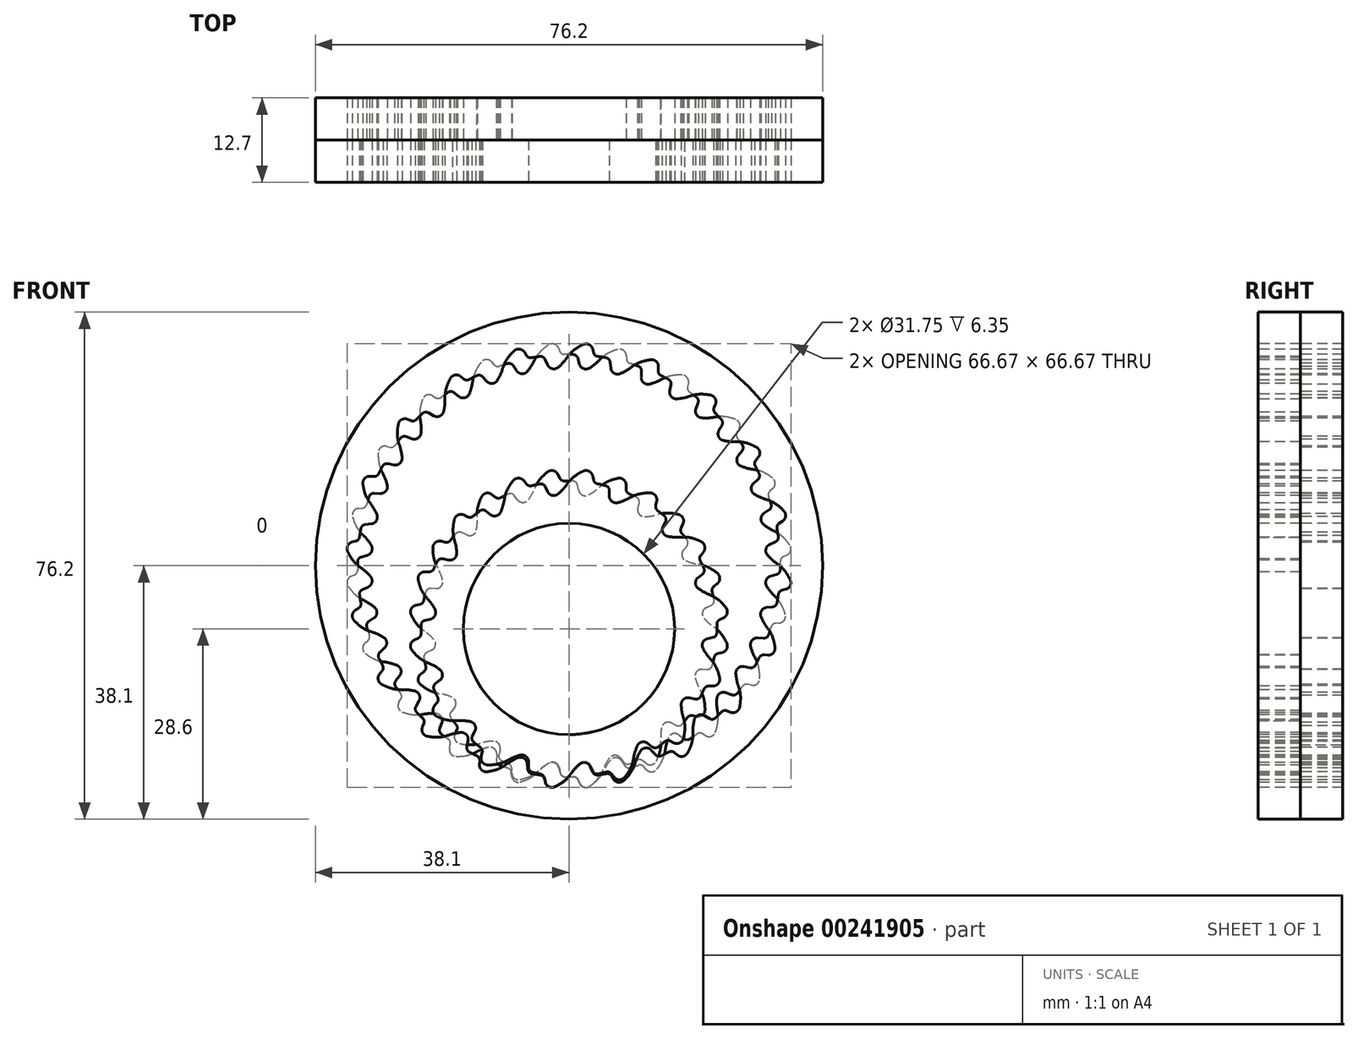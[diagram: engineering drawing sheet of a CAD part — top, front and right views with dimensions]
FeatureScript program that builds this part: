
annotation { "Feature Type Name" : "Feature", "Feature Type Description" : "" }
export const myFeature = defineFeature(function(context is Context, id is Id, definition is map)
    precondition{}
    {
        {
            var Q0;
            Q0=qCreatedBy(makeId("Front.planeOp"),FACE);
            var sketch = newSketch(context, id + "F0", { "sketchPlane" : qUnion([Q0])});
            skCircle(sketch, "E0", {"center": v(0, 0) * mm, "radius": 38.1 * mm});
            skCircle(sketch, "E1", {"center": v(0, 0) * mm, "radius": 31.75 * mm});
            skCircle(sketch, "E2", {"center": v(0, 0) * mm, "radius": 22.23 * mm});
            skCircle(sketch, "E3", {"center": v(0, 0) * mm, "radius": 15.88 * mm});
            skLineSegment(sketch, "E4", {"start": v(2.7, -19.53) * mm, "end": v(3.8, -21.9) * mm});
            skLineSegment(sketch, "E5", {"start": v(-3.3, -24.13) * mm, "end": v(-3.8, -21.9) * mm});
            skLineSegment(sketch, "E6", {"start": v(2.7, -29.06) * mm, "end": v(3.8, -31.52) * mm});
            skLineSegment(sketch, "E7", {"start": v(-3.3, -33.66) * mm, "end": v(-3.8, -31.52) * mm});
            skArc(sketch, "E8", {"start": v(2.7, -19.53) * mm, "mid": v(1.17, -20.7) * mm, "end": v(0, -22.23) * mm});
            skArc(sketch, "E9", {"start": v(-3.3, -24.13) * mm, "mid": v(-1.52, -23.4) * mm, "end": v(0, -22.23) * mm});
            skArc(sketch, "E10", {"start": v(-3.3, -33.66) * mm, "mid": v(-1.52, -32.92) * mm, "end": v(0, -31.75) * mm});
            skArc(sketch, "E11", {"start": v(2.7, -29.06) * mm, "mid": v(1.17, -30.22) * mm, "end": v(0, -31.75) * mm});
            skLineSegment(sketch, "E12.1.0", {"start": v(7.5, -23.17) * mm, "end": v(6.08, -21.38) * mm});
            skArc(sketch, "E12.1.1", {"start": v(7.5, -23.17) * mm, "mid": v(8.78, -21.74) * mm, "end": v(9.64, -20.02) * mm});
            skArc(sketch, "E12.1.2", {"start": v(10.9, -16.43) * mm, "mid": v(10.03, -18.14) * mm, "end": v(9.64, -20.02) * mm});
            skLineSegment(sketch, "E12.1.3", {"start": v(10.9, -16.43) * mm, "end": v(12.92, -18.08) * mm});
            skLineSegment(sketch, "E12.2.0", {"start": v(16.8, -17.62) * mm, "end": v(14.75, -16.62) * mm});
            skArc(sketch, "E12.2.1", {"start": v(16.8, -17.62) * mm, "mid": v(17.34, -15.78) * mm, "end": v(17.38, -13.86) * mm});
            skArc(sketch, "E12.2.2", {"start": v(16.95, -10.07) * mm, "mid": v(16.91, -12) * mm, "end": v(17.38, -13.86) * mm});
            skLineSegment(sketch, "E12.2.3", {"start": v(16.95, -10.07) * mm, "end": v(19.49, -10.69) * mm});
            skLineSegment(sketch, "E12.3.0", {"start": v(22.8, -8.59) * mm, "end": v(20.5, -8.57) * mm});
            skArc(sketch, "E12.3.1", {"start": v(22.8, -8.59) * mm, "mid": v(22.47, -6.7) * mm, "end": v(21.67, -4.95) * mm});
            skArc(sketch, "E12.3.2", {"start": v(19.64, -1.72) * mm, "mid": v(20.44, -3.47) * mm, "end": v(21.67, -4.95) * mm});
            skLineSegment(sketch, "E12.3.3", {"start": v(19.64, -1.72) * mm, "end": v(22.2, -1.17) * mm});
            skLineSegment(sketch, "E12.4.0", {"start": v(24.26, 2.15) * mm, "end": v(22.2, 1.17) * mm});
            skArc(sketch, "E12.4.1", {"start": v(24.26, 2.15) * mm, "mid": v(23.15, 3.72) * mm, "end": v(21.67, 4.95) * mm});
            skArc(sketch, "E12.4.2", {"start": v(18.44, 6.97) * mm, "mid": v(19.92, 5.74) * mm, "end": v(21.67, 4.95) * mm});
            skLineSegment(sketch, "E12.4.3", {"start": v(18.44, 6.97) * mm, "end": v(20.5, 8.57) * mm});
            skLineSegment(sketch, "E12.5.0", {"start": v(20.92, 12.47) * mm, "end": v(19.49, 10.69) * mm});
            skArc(sketch, "E12.5.1", {"start": v(20.92, 12.47) * mm, "mid": v(19.24, 13.4) * mm, "end": v(17.38, 13.86) * mm});
            skArc(sketch, "E12.5.2", {"start": v(13.6, 14.28) * mm, "mid": v(15.45, 13.82) * mm, "end": v(17.38, 13.86) * mm});
            skLineSegment(sketch, "E12.5.3", {"start": v(13.6, 14.28) * mm, "end": v(14.75, 16.62) * mm});
            skLineSegment(sketch, "E12.6.0", {"start": v(13.44, 20.3) * mm, "end": v(12.92, 18.08) * mm});
            skArc(sketch, "E12.6.1", {"start": v(13.44, 20.3) * mm, "mid": v(11.52, 20.42) * mm, "end": v(9.64, 20.02) * mm});
            skArc(sketch, "E12.6.2", {"start": v(6.05, 18.77) * mm, "mid": v(7.93, 19.16) * mm, "end": v(9.64, 20.02) * mm});
            skLineSegment(sketch, "E12.6.3", {"start": v(6.05, 18.77) * mm, "end": v(6.08, 21.38) * mm});
            skLineSegment(sketch, "E12.7.0", {"start": v(3.3, 24.13) * mm, "end": v(3.8, 21.9) * mm});
            skArc(sketch, "E12.7.1", {"start": v(3.3, 24.13) * mm, "mid": v(1.52, 23.4) * mm, "end": v(0, 22.23) * mm});
            skArc(sketch, "E12.7.2", {"start": v(-2.7, 19.53) * mm, "mid": v(-1.17, 20.7) * mm, "end": v(0, 22.22) * mm});
            skLineSegment(sketch, "E12.7.3", {"start": v(-2.7, 19.53) * mm, "end": v(-3.8, 21.9) * mm});
            skLineSegment(sketch, "E12.8.0", {"start": v(-7.5, 23.17) * mm, "end": v(-6.08, 21.38) * mm});
            skArc(sketch, "E12.8.1", {"start": v(-7.5, 23.17) * mm, "mid": v(-8.78, 21.74) * mm, "end": v(-9.64, 20.02) * mm});
            skArc(sketch, "E12.8.2", {"start": v(-10.9, 16.43) * mm, "mid": v(-10.03, 18.14) * mm, "end": v(-9.64, 20.02) * mm});
            skLineSegment(sketch, "E12.8.3", {"start": v(-10.9, 16.43) * mm, "end": v(-12.92, 18.08) * mm});
            skLineSegment(sketch, "E12.9.0", {"start": v(-16.8, 17.62) * mm, "end": v(-14.75, 16.62) * mm});
            skArc(sketch, "E12.9.1", {"start": v(-16.8, 17.62) * mm, "mid": v(-17.34, 15.78) * mm, "end": v(-17.38, 13.86) * mm});
            skArc(sketch, "E12.9.2", {"start": v(-16.95, 10.07) * mm, "mid": v(-16.91, 12) * mm, "end": v(-17.38, 13.86) * mm});
            skLineSegment(sketch, "E12.9.3", {"start": v(-16.95, 10.07) * mm, "end": v(-19.49, 10.69) * mm});
            skLineSegment(sketch, "E12.10.0", {"start": v(-22.8, 8.59) * mm, "end": v(-20.5, 8.57) * mm});
            skArc(sketch, "E12.10.1", {"start": v(-22.8, 8.59) * mm, "mid": v(-22.47, 6.7) * mm, "end": v(-21.67, 4.95) * mm});
            skArc(sketch, "E12.10.2", {"start": v(-19.64, 1.72) * mm, "mid": v(-20.44, 3.47) * mm, "end": v(-21.67, 4.95) * mm});
            skLineSegment(sketch, "E12.10.3", {"start": v(-19.64, 1.72) * mm, "end": v(-22.2, 1.17) * mm});
            skLineSegment(sketch, "E12.11.0", {"start": v(-24.26, -2.15) * mm, "end": v(-22.2, -1.17) * mm});
            skArc(sketch, "E12.11.1", {"start": v(-24.26, -2.15) * mm, "mid": v(-23.15, -3.72) * mm, "end": v(-21.67, -4.95) * mm});
            skArc(sketch, "E12.11.2", {"start": v(-18.44, -6.97) * mm, "mid": v(-19.92, -5.74) * mm, "end": v(-21.67, -4.95) * mm});
            skLineSegment(sketch, "E12.11.3", {"start": v(-18.44, -6.97) * mm, "end": v(-20.5, -8.57) * mm});
            skLineSegment(sketch, "E12.12.0", {"start": v(-20.92, -12.47) * mm, "end": v(-19.49, -10.69) * mm});
            skArc(sketch, "E12.12.1", {"start": v(-20.92, -12.47) * mm, "mid": v(-19.24, -13.4) * mm, "end": v(-17.38, -13.86) * mm});
            skArc(sketch, "E12.12.2", {"start": v(-13.6, -14.28) * mm, "mid": v(-15.45, -13.82) * mm, "end": v(-17.38, -13.86) * mm});
            skLineSegment(sketch, "E12.12.3", {"start": v(-13.6, -14.28) * mm, "end": v(-14.75, -16.62) * mm});
            skLineSegment(sketch, "E12.13.0", {"start": v(-13.44, -20.3) * mm, "end": v(-12.92, -18.08) * mm});
            skArc(sketch, "E12.13.1", {"start": v(-13.44, -20.3) * mm, "mid": v(-11.52, -20.42) * mm, "end": v(-9.64, -20.02) * mm});
            skArc(sketch, "E12.13.2", {"start": v(-6.05, -18.77) * mm, "mid": v(-7.93, -19.16) * mm, "end": v(-9.64, -20.02) * mm});
            skLineSegment(sketch, "E12.13.3", {"start": v(-6.05, -18.77) * mm, "end": v(-6.08, -21.38) * mm});
            skLineSegment(sketch, "E13.1.0", {"start": v(7.26, -33.03) * mm, "end": v(6.12, -31.15) * mm});
            skArc(sketch, "E13.1.1", {"start": v(7.26, -33.03) * mm, "mid": v(8.73, -31.78) * mm, "end": v(9.81, -30.2) * mm});
            skArc(sketch, "E13.1.2", {"start": v(11.54, -26.8) * mm, "mid": v(10.45, -28.38) * mm, "end": v(9.81, -30.2) * mm});
            skLineSegment(sketch, "E13.1.3", {"start": v(11.54, -26.8) * mm, "end": v(13.36, -28.8) * mm});
            skLineSegment(sketch, "E13.2.0", {"start": v(17.11, -29.17) * mm, "end": v(15.45, -27.74) * mm});
            skArc(sketch, "E13.2.1", {"start": v(17.11, -29.17) * mm, "mid": v(18.12, -27.53) * mm, "end": v(18.66, -25.69) * mm});
            skArc(sketch, "E13.2.2", {"start": v(19.26, -21.92) * mm, "mid": v(18.7, -23.77) * mm, "end": v(18.66, -25.69) * mm});
            skLineSegment(sketch, "E13.2.3", {"start": v(19.26, -21.92) * mm, "end": v(21.6, -23.27) * mm});
            skLineSegment(sketch, "E13.3.0", {"start": v(25.29, -22.45) * mm, "end": v(23.27, -21.6) * mm});
            skArc(sketch, "E13.3.1", {"start": v(25.29, -22.45) * mm, "mid": v(25.74, -20.58) * mm, "end": v(25.69, -18.66) * mm});
            skArc(sketch, "E13.3.2", {"start": v(25.1, -14.9) * mm, "mid": v(25.14, -16.82) * mm, "end": v(25.69, -18.66) * mm});
            skLineSegment(sketch, "E13.3.3", {"start": v(25.1, -14.9) * mm, "end": v(27.74, -15.45) * mm});
            skLineSegment(sketch, "E13.4.0", {"start": v(30.99, -13.54) * mm, "end": v(28.8, -13.36) * mm});
            skArc(sketch, "E13.4.1", {"start": v(30.99, -13.54) * mm, "mid": v(30.84, -11.62) * mm, "end": v(30.2, -9.81) * mm});
            skArc(sketch, "E13.4.2", {"start": v(28.47, -6.42) * mm, "mid": v(29.1, -8.23) * mm, "end": v(30.2, -9.81) * mm});
            skLineSegment(sketch, "E13.4.3", {"start": v(28.47, -6.42) * mm, "end": v(31.15, -6.12) * mm});
            skLineSegment(sketch, "E13.5.0", {"start": v(33.66, -3.3) * mm, "end": v(31.52, -3.8) * mm});
            skArc(sketch, "E13.5.1", {"start": v(33.66, -3.3) * mm, "mid": v(32.92, -1.52) * mm, "end": v(31.75, 0) * mm});
            skArc(sketch, "E13.5.2", {"start": v(29.06, 2.7) * mm, "mid": v(30.22, 1.17) * mm, "end": v(31.75, 0) * mm});
            skLineSegment(sketch, "E13.5.3", {"start": v(29.06, 2.7) * mm, "end": v(31.52, 3.8) * mm});
            skLineSegment(sketch, "E13.6.0", {"start": v(33.03, 7.26) * mm, "end": v(31.15, 6.12) * mm});
            skArc(sketch, "E13.6.1", {"start": v(33.03, 7.26) * mm, "mid": v(31.78, 8.73) * mm, "end": v(30.2, 9.81) * mm});
            skArc(sketch, "E13.6.2", {"start": v(26.8, 11.54) * mm, "mid": v(28.38, 10.45) * mm, "end": v(30.2, 9.81) * mm});
            skLineSegment(sketch, "E13.6.3", {"start": v(26.8, 11.54) * mm, "end": v(28.8, 13.36) * mm});
            skLineSegment(sketch, "E13.7.0", {"start": v(29.17, 17.11) * mm, "end": v(27.74, 15.45) * mm});
            skArc(sketch, "E13.7.1", {"start": v(29.17, 17.11) * mm, "mid": v(27.53, 18.12) * mm, "end": v(25.69, 18.66) * mm});
            skArc(sketch, "E13.7.2", {"start": v(21.92, 19.26) * mm, "mid": v(23.77, 18.7) * mm, "end": v(25.69, 18.66) * mm});
            skLineSegment(sketch, "E13.7.3", {"start": v(21.92, 19.26) * mm, "end": v(23.27, 21.6) * mm});
            skLineSegment(sketch, "E13.8.0", {"start": v(22.45, 25.29) * mm, "end": v(21.6, 23.27) * mm});
            skArc(sketch, "E13.8.1", {"start": v(22.45, 25.29) * mm, "mid": v(20.58, 25.74) * mm, "end": v(18.66, 25.69) * mm});
            skArc(sketch, "E13.8.2", {"start": v(14.9, 25.1) * mm, "mid": v(16.82, 25.14) * mm, "end": v(18.66, 25.69) * mm});
            skLineSegment(sketch, "E13.8.3", {"start": v(14.9, 25.1) * mm, "end": v(15.45, 27.74) * mm});
            skLineSegment(sketch, "E13.9.0", {"start": v(13.54, 30.99) * mm, "end": v(13.36, 28.8) * mm});
            skArc(sketch, "E13.9.1", {"start": v(13.54, 30.99) * mm, "mid": v(11.62, 30.84) * mm, "end": v(9.81, 30.2) * mm});
            skArc(sketch, "E13.9.2", {"start": v(6.42, 28.47) * mm, "mid": v(8.23, 29.1) * mm, "end": v(9.81, 30.2) * mm});
            skLineSegment(sketch, "E13.9.3", {"start": v(6.42, 28.47) * mm, "end": v(6.12, 31.15) * mm});
            skLineSegment(sketch, "E13.10.0", {"start": v(3.3, 33.66) * mm, "end": v(3.8, 31.52) * mm});
            skArc(sketch, "E13.10.1", {"start": v(3.3, 33.66) * mm, "mid": v(1.52, 32.92) * mm, "end": v(0, 31.75) * mm});
            skArc(sketch, "E13.10.2", {"start": v(-2.7, 29.06) * mm, "mid": v(-1.17, 30.22) * mm, "end": v(0, 31.75) * mm});
            skLineSegment(sketch, "E13.10.3", {"start": v(-2.7, 29.06) * mm, "end": v(-3.8, 31.52) * mm});
            skLineSegment(sketch, "E13.11.0", {"start": v(-7.26, 33.03) * mm, "end": v(-6.12, 31.15) * mm});
            skArc(sketch, "E13.11.1", {"start": v(-7.26, 33.03) * mm, "mid": v(-8.73, 31.78) * mm, "end": v(-9.81, 30.2) * mm});
            skArc(sketch, "E13.11.2", {"start": v(-11.54, 26.8) * mm, "mid": v(-10.45, 28.38) * mm, "end": v(-9.81, 30.2) * mm});
            skLineSegment(sketch, "E13.11.3", {"start": v(-11.54, 26.8) * mm, "end": v(-13.36, 28.8) * mm});
            skLineSegment(sketch, "E13.12.0", {"start": v(-17.11, 29.17) * mm, "end": v(-15.45, 27.74) * mm});
            skArc(sketch, "E13.12.1", {"start": v(-17.11, 29.17) * mm, "mid": v(-18.12, 27.53) * mm, "end": v(-18.66, 25.69) * mm});
            skArc(sketch, "E13.12.2", {"start": v(-19.26, 21.92) * mm, "mid": v(-18.7, 23.77) * mm, "end": v(-18.66, 25.69) * mm});
            skLineSegment(sketch, "E13.12.3", {"start": v(-19.26, 21.92) * mm, "end": v(-21.6, 23.27) * mm});
            skLineSegment(sketch, "E13.13.0", {"start": v(-25.29, 22.45) * mm, "end": v(-23.27, 21.6) * mm});
            skArc(sketch, "E13.13.1", {"start": v(-25.29, 22.45) * mm, "mid": v(-25.74, 20.58) * mm, "end": v(-25.69, 18.66) * mm});
            skArc(sketch, "E13.13.2", {"start": v(-25.1, 14.9) * mm, "mid": v(-25.14, 16.82) * mm, "end": v(-25.69, 18.66) * mm});
            skLineSegment(sketch, "E13.13.3", {"start": v(-25.1, 14.9) * mm, "end": v(-27.74, 15.45) * mm});
            skLineSegment(sketch, "E13.14.0", {"start": v(-30.99, 13.54) * mm, "end": v(-28.8, 13.36) * mm});
            skArc(sketch, "E13.14.1", {"start": v(-30.99, 13.54) * mm, "mid": v(-30.84, 11.62) * mm, "end": v(-30.2, 9.81) * mm});
            skArc(sketch, "E13.14.2", {"start": v(-28.47, 6.42) * mm, "mid": v(-29.1, 8.23) * mm, "end": v(-30.2, 9.81) * mm});
            skLineSegment(sketch, "E13.14.3", {"start": v(-28.47, 6.42) * mm, "end": v(-31.15, 6.12) * mm});
            skLineSegment(sketch, "E13.15.0", {"start": v(-33.66, 3.3) * mm, "end": v(-31.52, 3.8) * mm});
            skArc(sketch, "E13.15.1", {"start": v(-33.66, 3.3) * mm, "mid": v(-32.92, 1.52) * mm, "end": v(-31.75, 0) * mm});
            skArc(sketch, "E13.15.2", {"start": v(-29.06, -2.7) * mm, "mid": v(-30.22, -1.17) * mm, "end": v(-31.75, 0) * mm});
            skLineSegment(sketch, "E13.15.3", {"start": v(-29.06, -2.7) * mm, "end": v(-31.52, -3.8) * mm});
            skLineSegment(sketch, "E13.16.0", {"start": v(-33.03, -7.26) * mm, "end": v(-31.15, -6.12) * mm});
            skArc(sketch, "E13.16.1", {"start": v(-33.03, -7.26) * mm, "mid": v(-31.78, -8.73) * mm, "end": v(-30.2, -9.81) * mm});
            skArc(sketch, "E13.16.2", {"start": v(-26.8, -11.54) * mm, "mid": v(-28.38, -10.45) * mm, "end": v(-30.2, -9.81) * mm});
            skLineSegment(sketch, "E13.16.3", {"start": v(-26.8, -11.54) * mm, "end": v(-28.8, -13.36) * mm});
            skLineSegment(sketch, "E13.17.0", {"start": v(-29.17, -17.11) * mm, "end": v(-27.74, -15.45) * mm});
            skArc(sketch, "E13.17.1", {"start": v(-29.17, -17.11) * mm, "mid": v(-27.53, -18.12) * mm, "end": v(-25.69, -18.66) * mm});
            skArc(sketch, "E13.17.2", {"start": v(-21.92, -19.26) * mm, "mid": v(-23.77, -18.7) * mm, "end": v(-25.69, -18.66) * mm});
            skLineSegment(sketch, "E13.17.3", {"start": v(-21.92, -19.26) * mm, "end": v(-23.27, -21.6) * mm});
            skLineSegment(sketch, "E13.18.0", {"start": v(-22.45, -25.29) * mm, "end": v(-21.6, -23.27) * mm});
            skArc(sketch, "E13.18.1", {"start": v(-22.45, -25.29) * mm, "mid": v(-20.58, -25.74) * mm, "end": v(-18.66, -25.69) * mm});
            skArc(sketch, "E13.18.2", {"start": v(-14.9, -25.1) * mm, "mid": v(-16.82, -25.14) * mm, "end": v(-18.66, -25.69) * mm});
            skLineSegment(sketch, "E13.18.3", {"start": v(-14.9, -25.1) * mm, "end": v(-15.45, -27.74) * mm});
            skLineSegment(sketch, "E13.19.0", {"start": v(-13.54, -30.99) * mm, "end": v(-13.36, -28.8) * mm});
            skArc(sketch, "E13.19.1", {"start": v(-13.54, -30.99) * mm, "mid": v(-11.62, -30.84) * mm, "end": v(-9.81, -30.2) * mm});
            skArc(sketch, "E13.19.2", {"start": v(-6.42, -28.47) * mm, "mid": v(-8.23, -29.1) * mm, "end": v(-9.81, -30.2) * mm});
            skLineSegment(sketch, "E13.19.3", {"start": v(-6.42, -28.47) * mm, "end": v(-6.12, -31.15) * mm});
            skLineSegment(sketch, "E14", {"start": v(0, 31.75) * mm, "end": v(3.3, 33.66) * mm});
            skLineSegment(sketch, "E15", {"start": v(0, 22.23) * mm, "end": v(-2.7, 19.53) * mm});
            skSolve(sketch);
        }
        {
            var Q0;
            Q0=makeQuery(id+"F0.imprint","IMPRINT",FACE,{"disambiguationData":[TD([[makeQuery(id+"F0.imprint","IMPRINT",EDGE,{"derivedFrom":sQuery(id+"F0.wireOp",EDGE,"E0")}),1.0]])]});
            var Q1;
            {var subQ0=sQuery(id+"F0.wireOp",EDGE,"E13.10.2");Q1=makeQuery(id+"F0.imprint","IMPRINT",FACE,{"disambiguationData":[TD([[makeQuery(id+"F0.imprint","IMPRINT",EDGE,{"derivedFrom":subQ0}),1.0]])]});}
            var Q2;
            {var subQ0=sQuery(id+"F0.wireOp",EDGE,"E13.9.2");Q2=makeQuery(id+"F0.imprint","IMPRINT",FACE,{"disambiguationData":[TD([[makeQuery(id+"F0.imprint","IMPRINT",EDGE,{"derivedFrom":subQ0}),1.0]])]});}
            var Q3;
            {var subQ0=sQuery(id+"F0.wireOp",EDGE,"E13.8.2");Q3=makeQuery(id+"F0.imprint","IMPRINT",FACE,{"disambiguationData":[TD([[makeQuery(id+"F0.imprint","IMPRINT",EDGE,{"derivedFrom":subQ0}),1.0]])]});}
            var Q4;
            {var subQ0=sQuery(id+"F0.wireOp",EDGE,"E13.7.2");Q4=makeQuery(id+"F0.imprint","IMPRINT",FACE,{"disambiguationData":[TD([[makeQuery(id+"F0.imprint","IMPRINT",EDGE,{"derivedFrom":subQ0}),1.0]])]});}
            var Q5;
            {var subQ0=sQuery(id+"F0.wireOp",EDGE,"E13.12.2");Q5=makeQuery(id+"F0.imprint","IMPRINT",FACE,{"disambiguationData":[TD([[makeQuery(id+"F0.imprint","IMPRINT",EDGE,{"derivedFrom":subQ0}),1.0]])]});}
            var Q6;
            {var subQ0=sQuery(id+"F0.wireOp",EDGE,"E13.11.2");Q6=makeQuery(id+"F0.imprint","IMPRINT",FACE,{"disambiguationData":[TD([[makeQuery(id+"F0.imprint","IMPRINT",EDGE,{"derivedFrom":subQ0}),1.0]])]});}
            var Q7;
            {var subQ0=sQuery(id+"F0.wireOp",EDGE,"E13.13.2");Q7=makeQuery(id+"F0.imprint","IMPRINT",FACE,{"disambiguationData":[TD([[makeQuery(id+"F0.imprint","IMPRINT",EDGE,{"derivedFrom":subQ0}),1.0]])]});}
            var Q8;
            {var subQ0=sQuery(id+"F0.wireOp",EDGE,"E13.14.2");Q8=makeQuery(id+"F0.imprint","IMPRINT",FACE,{"disambiguationData":[TD([[makeQuery(id+"F0.imprint","IMPRINT",EDGE,{"derivedFrom":subQ0}),1.0]])]});}
            var Q9;
            {var subQ0=sQuery(id+"F0.wireOp",EDGE,"E13.15.2");Q9=makeQuery(id+"F0.imprint","IMPRINT",FACE,{"disambiguationData":[TD([[makeQuery(id+"F0.imprint","IMPRINT",EDGE,{"derivedFrom":subQ0}),1.0]])]});}
            var Q10;
            {var subQ0=sQuery(id+"F0.wireOp",EDGE,"E13.16.2");Q10=makeQuery(id+"F0.imprint","IMPRINT",FACE,{"disambiguationData":[TD([[makeQuery(id+"F0.imprint","IMPRINT",EDGE,{"derivedFrom":subQ0}),1.0]])]});}
            var Q11;
            {var subQ0=sQuery(id+"F0.wireOp",EDGE,"E13.17.2");Q11=makeQuery(id+"F0.imprint","IMPRINT",FACE,{"disambiguationData":[TD([[makeQuery(id+"F0.imprint","IMPRINT",EDGE,{"derivedFrom":subQ0}),1.0]])]});}
            var Q12;
            {var subQ0=sQuery(id+"F0.wireOp",EDGE,"E13.18.2");Q12=makeQuery(id+"F0.imprint","IMPRINT",FACE,{"disambiguationData":[TD([[makeQuery(id+"F0.imprint","IMPRINT",EDGE,{"derivedFrom":subQ0}),1.0]])]});}
            var Q13;
            {var subQ0=sQuery(id+"F0.wireOp",EDGE,"E13.19.2");Q13=makeQuery(id+"F0.imprint","IMPRINT",FACE,{"disambiguationData":[TD([[makeQuery(id+"F0.imprint","IMPRINT",EDGE,{"derivedFrom":subQ0}),1.0]])]});}
            var Q14;
            {var subQ0=sQuery(id+"F0.wireOp",EDGE,"E6");Q14=makeQuery(id+"F0.imprint","IMPRINT",FACE,{"disambiguationData":[TD([[makeQuery(id+"F0.imprint","IMPRINT",EDGE,{"derivedFrom":subQ0}),-1.0]])]});}
            var Q15;
            {var subQ0=sQuery(id+"F0.wireOp",EDGE,"E13.1.2");Q15=makeQuery(id+"F0.imprint","IMPRINT",FACE,{"disambiguationData":[TD([[makeQuery(id+"F0.imprint","IMPRINT",EDGE,{"derivedFrom":subQ0}),1.0]])]});}
            var Q16;
            {var subQ0=sQuery(id+"F0.wireOp",EDGE,"E13.2.2");Q16=makeQuery(id+"F0.imprint","IMPRINT",FACE,{"disambiguationData":[TD([[makeQuery(id+"F0.imprint","IMPRINT",EDGE,{"derivedFrom":subQ0}),1.0]])]});}
            var Q17;
            {var subQ0=sQuery(id+"F0.wireOp",EDGE,"E13.3.2");Q17=makeQuery(id+"F0.imprint","IMPRINT",FACE,{"disambiguationData":[TD([[makeQuery(id+"F0.imprint","IMPRINT",EDGE,{"derivedFrom":subQ0}),1.0]])]});}
            var Q18;
            {var subQ0=sQuery(id+"F0.wireOp",EDGE,"E13.4.2");Q18=makeQuery(id+"F0.imprint","IMPRINT",FACE,{"disambiguationData":[TD([[makeQuery(id+"F0.imprint","IMPRINT",EDGE,{"derivedFrom":subQ0}),1.0]])]});}
            var Q19;
            {var subQ0=sQuery(id+"F0.wireOp",EDGE,"E13.5.2");Q19=makeQuery(id+"F0.imprint","IMPRINT",FACE,{"disambiguationData":[TD([[makeQuery(id+"F0.imprint","IMPRINT",EDGE,{"derivedFrom":subQ0}),1.0]])]});}
            var Q20;
            {var subQ0=sQuery(id+"F0.wireOp",EDGE,"E13.6.2");Q20=makeQuery(id+"F0.imprint","IMPRINT",FACE,{"disambiguationData":[TD([[makeQuery(id+"F0.imprint","IMPRINT",EDGE,{"derivedFrom":subQ0}),1.0]])]});}
            extrude(context, id + "F1", {"entities" : qUnion([Q0, Q1, Q2, Q3, Q4, Q5, Q6, Q7, Q8, Q9, Q10, Q11, Q12, Q13, Q14, Q15, Q16, Q17, Q18, Q19, Q20]), "oppositeDirection" : true, "depth" : 6.35 * mm});
        }
        {
            var Q0;
            Q0=makeQuery(id+"F0.imprint","IMPRINT",FACE,{"disambiguationData":[TD([[makeQuery(id+"F0.imprint","IMPRINT",EDGE,{"derivedFrom":sQuery(id+"F0.wireOp",EDGE,"E3")}),-1.0]])]});
            var Q1;
            {var subQ0=sQuery(id+"F0.wireOp",EDGE,"E12.8.0");Q1=makeQuery(id+"F0.imprint","IMPRINT",FACE,{"disambiguationData":[TD([[makeQuery(id+"F0.imprint","IMPRINT",EDGE,{"derivedFrom":subQ0}),-1.0]])]});}
            var Q2;
            {var subQ0=sQuery(id+"F0.wireOp",EDGE,"E12.7.0");Q2=makeQuery(id+"F0.imprint","IMPRINT",FACE,{"disambiguationData":[TD([[makeQuery(id+"F0.imprint","IMPRINT",EDGE,{"derivedFrom":subQ0}),-1.0]])]});}
            var Q3;
            {var subQ0=sQuery(id+"F0.wireOp",EDGE,"E12.6.0");Q3=makeQuery(id+"F0.imprint","IMPRINT",FACE,{"disambiguationData":[TD([[makeQuery(id+"F0.imprint","IMPRINT",EDGE,{"derivedFrom":subQ0}),-1.0]])]});}
            var Q4;
            {var subQ0=sQuery(id+"F0.wireOp",EDGE,"E12.5.0");Q4=makeQuery(id+"F0.imprint","IMPRINT",FACE,{"disambiguationData":[TD([[makeQuery(id+"F0.imprint","IMPRINT",EDGE,{"derivedFrom":subQ0}),-1.0]])]});}
            var Q5;
            {var subQ0=sQuery(id+"F0.wireOp",EDGE,"E12.9.0");Q5=makeQuery(id+"F0.imprint","IMPRINT",FACE,{"disambiguationData":[TD([[makeQuery(id+"F0.imprint","IMPRINT",EDGE,{"derivedFrom":subQ0}),-1.0]])]});}
            var Q6;
            {var subQ0=sQuery(id+"F0.wireOp",EDGE,"E12.10.0");Q6=makeQuery(id+"F0.imprint","IMPRINT",FACE,{"disambiguationData":[TD([[makeQuery(id+"F0.imprint","IMPRINT",EDGE,{"derivedFrom":subQ0}),-1.0]])]});}
            var Q7;
            {var subQ0=sQuery(id+"F0.wireOp",EDGE,"E12.11.0");Q7=makeQuery(id+"F0.imprint","IMPRINT",FACE,{"disambiguationData":[TD([[makeQuery(id+"F0.imprint","IMPRINT",EDGE,{"derivedFrom":subQ0}),-1.0]])]});}
            var Q8;
            {var subQ0=sQuery(id+"F0.wireOp",EDGE,"E12.12.0");Q8=makeQuery(id+"F0.imprint","IMPRINT",FACE,{"disambiguationData":[TD([[makeQuery(id+"F0.imprint","IMPRINT",EDGE,{"derivedFrom":subQ0}),-1.0]])]});}
            var Q9;
            {var subQ0=sQuery(id+"F0.wireOp",EDGE,"E12.13.0");Q9=makeQuery(id+"F0.imprint","IMPRINT",FACE,{"disambiguationData":[TD([[makeQuery(id+"F0.imprint","IMPRINT",EDGE,{"derivedFrom":subQ0}),-1.0]])]});}
            var Q10;
            {var subQ0=sQuery(id+"F0.wireOp",EDGE,"E5");Q10=makeQuery(id+"F0.imprint","IMPRINT",FACE,{"disambiguationData":[TD([[makeQuery(id+"F0.imprint","IMPRINT",EDGE,{"derivedFrom":subQ0}),-1.0]])]});}
            var Q11;
            {var subQ0=sQuery(id+"F0.wireOp",EDGE,"E12.1.0");Q11=makeQuery(id+"F0.imprint","IMPRINT",FACE,{"disambiguationData":[TD([[makeQuery(id+"F0.imprint","IMPRINT",EDGE,{"derivedFrom":subQ0}),-1.0]])]});}
            var Q12;
            {var subQ0=sQuery(id+"F0.wireOp",EDGE,"E12.2.0");Q12=makeQuery(id+"F0.imprint","IMPRINT",FACE,{"disambiguationData":[TD([[makeQuery(id+"F0.imprint","IMPRINT",EDGE,{"derivedFrom":subQ0}),-1.0]])]});}
            var Q13;
            {var subQ0=sQuery(id+"F0.wireOp",EDGE,"E12.3.0");Q13=makeQuery(id+"F0.imprint","IMPRINT",FACE,{"disambiguationData":[TD([[makeQuery(id+"F0.imprint","IMPRINT",EDGE,{"derivedFrom":subQ0}),-1.0]])]});}
            var Q14;
            {var subQ0=sQuery(id+"F0.wireOp",EDGE,"E12.4.0");Q14=makeQuery(id+"F0.imprint","IMPRINT",FACE,{"disambiguationData":[TD([[makeQuery(id+"F0.imprint","IMPRINT",EDGE,{"derivedFrom":subQ0}),-1.0]])]});}
            extrude(context, id + "F2", {"entities" : qUnion([Q0, Q1, Q2, Q3, Q4, Q5, Q6, Q7, Q8, Q9, Q10, Q11, Q12, Q13, Q14]), "oppositeDirection" : true, "depth" : 6.35 * mm});
        }
        {
            var Q0;
            Q0=makeQuery(id+"F2.opExtrude","SWEPT_EDGE",EDGE,{"disambiguationData":[OSD([sQuery(id+"F0.wireOp",EDGE,"E2"),sQuery(id+"F0.wireOp",EDGE,"E8"),sQuery(id+"F0.wireOp",EDGE,"E9")])]});
            var Q1;
            Q1=makeQuery(id+"F2.opExtrude","SWEPT_EDGE",EDGE,{"disambiguationData":[OSD([sQuery(id+"F0.wireOp",EDGE,"E2"),sQuery(id+"F0.wireOp",EDGE,"E12.1.1"),sQuery(id+"F0.wireOp",EDGE,"E12.1.2")])]});
            var Q2;
            Q2=makeQuery(id+"F2.opExtrude","SWEPT_EDGE",EDGE,{"disambiguationData":[OSD([sQuery(id+"F0.wireOp",EDGE,"E2"),sQuery(id+"F0.wireOp",EDGE,"E12.13.1"),sQuery(id+"F0.wireOp",EDGE,"E12.13.2")])]});
            var Q3;
            Q3=makeQuery(id+"F1.opExtrude","SWEPT_EDGE",EDGE,{"disambiguationData":[OSD([sQuery(id+"F0.wireOp",EDGE,"E1"),sQuery(id+"F0.wireOp",EDGE,"E13.1.1"),sQuery(id+"F0.wireOp",EDGE,"E13.1.2")])]});
            var Q4;
            Q4=makeQuery(id+"F1.opExtrude","SWEPT_EDGE",EDGE,{"disambiguationData":[OSD([sQuery(id+"F0.wireOp",EDGE,"E1"),sQuery(id+"F0.wireOp",EDGE,"E10"),sQuery(id+"F0.wireOp",EDGE,"E11")])]});
            var Q5;
            Q5=makeQuery(id+"F1.opExtrude","SWEPT_EDGE",EDGE,{"disambiguationData":[OSD([sQuery(id+"F0.wireOp",EDGE,"E1"),sQuery(id+"F0.wireOp",EDGE,"E13.19.1"),sQuery(id+"F0.wireOp",EDGE,"E13.19.2")])]});
            var Q6;
            Q6=makeQuery(id+"F1.opExtrude","SWEPT_EDGE",EDGE,{"disambiguationData":[OSD([sQuery(id+"F0.wireOp",EDGE,"E1"),sQuery(id+"F0.wireOp",EDGE,"E13.18.1"),sQuery(id+"F0.wireOp",EDGE,"E13.18.2")])]});
            var Q7;
            Q7=makeQuery(id+"F1.opExtrude","SWEPT_EDGE",EDGE,{"disambiguationData":[OSD([sQuery(id+"F0.wireOp",EDGE,"E1"),sQuery(id+"F0.wireOp",EDGE,"E13.17.1"),sQuery(id+"F0.wireOp",EDGE,"E13.17.2")])]});
            var Q8;
            Q8=makeQuery(id+"F1.opExtrude","SWEPT_EDGE",EDGE,{"disambiguationData":[OSD([sQuery(id+"F0.wireOp",EDGE,"E1"),sQuery(id+"F0.wireOp",EDGE,"E13.2.1"),sQuery(id+"F0.wireOp",EDGE,"E13.2.2")])]});
            var Q9;
            Q9=makeQuery(id+"F1.opExtrude","SWEPT_EDGE",EDGE,{"disambiguationData":[OSD([sQuery(id+"F0.wireOp",EDGE,"E1"),sQuery(id+"F0.wireOp",EDGE,"E13.3.1"),sQuery(id+"F0.wireOp",EDGE,"E13.3.2")])]});
            var Q10;
            Q10=makeQuery(id+"F1.opExtrude","SWEPT_EDGE",EDGE,{"disambiguationData":[OSD([sQuery(id+"F0.wireOp",EDGE,"E1"),sQuery(id+"F0.wireOp",EDGE,"E13.4.1"),sQuery(id+"F0.wireOp",EDGE,"E13.4.2")])]});
            var Q11;
            Q11=makeQuery(id+"F1.opExtrude","SWEPT_EDGE",EDGE,{"disambiguationData":[OSD([sQuery(id+"F0.wireOp",EDGE,"E1"),sQuery(id+"F0.wireOp",EDGE,"E13.5.1"),sQuery(id+"F0.wireOp",EDGE,"E13.5.2")])]});
            var Q12;
            Q12=makeQuery(id+"F1.opExtrude","SWEPT_EDGE",EDGE,{"disambiguationData":[OSD([sQuery(id+"F0.wireOp",EDGE,"E1"),sQuery(id+"F0.wireOp",EDGE,"E13.6.1"),sQuery(id+"F0.wireOp",EDGE,"E13.6.2")])]});
            var Q13;
            Q13=makeQuery(id+"F1.opExtrude","SWEPT_EDGE",EDGE,{"disambiguationData":[OSD([sQuery(id+"F0.wireOp",EDGE,"E1"),sQuery(id+"F0.wireOp",EDGE,"E13.7.1"),sQuery(id+"F0.wireOp",EDGE,"E13.7.2")])]});
            var Q14;
            Q14=makeQuery(id+"F1.opExtrude","SWEPT_EDGE",EDGE,{"disambiguationData":[OSD([sQuery(id+"F0.wireOp",EDGE,"E1"),sQuery(id+"F0.wireOp",EDGE,"E13.8.1"),sQuery(id+"F0.wireOp",EDGE,"E13.8.2")])]});
            var Q15;
            Q15=makeQuery(id+"F1.opExtrude","SWEPT_EDGE",EDGE,{"disambiguationData":[OSD([sQuery(id+"F0.wireOp",EDGE,"E1"),sQuery(id+"F0.wireOp",EDGE,"E13.9.1"),sQuery(id+"F0.wireOp",EDGE,"E13.9.2")])]});
            var Q16;
            Q16=makeQuery(id+"F1.opExtrude","SWEPT_EDGE",EDGE,{"disambiguationData":[OSD([sQuery(id+"F0.wireOp",EDGE,"E1"),sQuery(id+"F0.wireOp",EDGE,"E13.10.1"),sQuery(id+"F0.wireOp",EDGE,"E13.10.2")])]});
            var Q17;
            Q17=makeQuery(id+"F1.opExtrude","SWEPT_EDGE",EDGE,{"disambiguationData":[OSD([sQuery(id+"F0.wireOp",EDGE,"E1"),sQuery(id+"F0.wireOp",EDGE,"E13.11.1"),sQuery(id+"F0.wireOp",EDGE,"E13.11.2")])]});
            var Q18;
            Q18=makeQuery(id+"F1.opExtrude","SWEPT_EDGE",EDGE,{"disambiguationData":[OSD([sQuery(id+"F0.wireOp",EDGE,"E1"),sQuery(id+"F0.wireOp",EDGE,"E13.12.1"),sQuery(id+"F0.wireOp",EDGE,"E13.12.2")])]});
            var Q19;
            Q19=makeQuery(id+"F1.opExtrude","SWEPT_EDGE",EDGE,{"disambiguationData":[OSD([sQuery(id+"F0.wireOp",EDGE,"E1"),sQuery(id+"F0.wireOp",EDGE,"E13.13.1"),sQuery(id+"F0.wireOp",EDGE,"E13.13.2")])]});
            var Q20;
            Q20=makeQuery(id+"F1.opExtrude","SWEPT_EDGE",EDGE,{"disambiguationData":[OSD([sQuery(id+"F0.wireOp",EDGE,"E1"),sQuery(id+"F0.wireOp",EDGE,"E13.14.1"),sQuery(id+"F0.wireOp",EDGE,"E13.14.2")])]});
            var Q21;
            Q21=makeQuery(id+"F1.opExtrude","SWEPT_EDGE",EDGE,{"disambiguationData":[OSD([sQuery(id+"F0.wireOp",EDGE,"E1"),sQuery(id+"F0.wireOp",EDGE,"E13.15.1"),sQuery(id+"F0.wireOp",EDGE,"E13.15.2")])]});
            var Q22;
            Q22=makeQuery(id+"F1.opExtrude","SWEPT_EDGE",EDGE,{"disambiguationData":[OSD([sQuery(id+"F0.wireOp",EDGE,"E1"),sQuery(id+"F0.wireOp",EDGE,"E13.16.1"),sQuery(id+"F0.wireOp",EDGE,"E13.16.2")])]});
            var Q23;
            Q23=makeQuery(id+"F2.opExtrude","SWEPT_EDGE",EDGE,{"disambiguationData":[OSD([sQuery(id+"F0.wireOp",EDGE,"E2"),sQuery(id+"F0.wireOp",EDGE,"E12.2.1"),sQuery(id+"F0.wireOp",EDGE,"E12.2.2")])]});
            var Q24;
            Q24=makeQuery(id+"F2.opExtrude","SWEPT_EDGE",EDGE,{"disambiguationData":[OSD([sQuery(id+"F0.wireOp",EDGE,"E2"),sQuery(id+"F0.wireOp",EDGE,"E12.12.1"),sQuery(id+"F0.wireOp",EDGE,"E12.12.2")])]});
            var Q25;
            Q25=makeQuery(id+"F2.opExtrude","SWEPT_EDGE",EDGE,{"disambiguationData":[OSD([sQuery(id+"F0.wireOp",EDGE,"E2"),sQuery(id+"F0.wireOp",EDGE,"E12.11.1"),sQuery(id+"F0.wireOp",EDGE,"E12.11.2")])]});
            var Q26;
            Q26=makeQuery(id+"F2.opExtrude","SWEPT_EDGE",EDGE,{"disambiguationData":[OSD([sQuery(id+"F0.wireOp",EDGE,"E2"),sQuery(id+"F0.wireOp",EDGE,"E12.10.1"),sQuery(id+"F0.wireOp",EDGE,"E12.10.2")])]});
            var Q27;
            Q27=makeQuery(id+"F2.opExtrude","SWEPT_EDGE",EDGE,{"disambiguationData":[OSD([sQuery(id+"F0.wireOp",EDGE,"E2"),sQuery(id+"F0.wireOp",EDGE,"E12.9.1"),sQuery(id+"F0.wireOp",EDGE,"E12.9.2")])]});
            var Q28;
            Q28=makeQuery(id+"F2.opExtrude","SWEPT_EDGE",EDGE,{"disambiguationData":[OSD([sQuery(id+"F0.wireOp",EDGE,"E2"),sQuery(id+"F0.wireOp",EDGE,"E12.8.1"),sQuery(id+"F0.wireOp",EDGE,"E12.8.2")])]});
            var Q29;
            Q29=makeQuery(id+"F2.opExtrude","SWEPT_EDGE",EDGE,{"disambiguationData":[OSD([sQuery(id+"F0.wireOp",EDGE,"E2"),sQuery(id+"F0.wireOp",EDGE,"E12.7.1"),sQuery(id+"F0.wireOp",EDGE,"E12.7.2")])]});
            var Q30;
            Q30=makeQuery(id+"F2.opExtrude","SWEPT_EDGE",EDGE,{"disambiguationData":[OSD([sQuery(id+"F0.wireOp",EDGE,"E2"),sQuery(id+"F0.wireOp",EDGE,"E12.6.1"),sQuery(id+"F0.wireOp",EDGE,"E12.6.2")])]});
            var Q31;
            Q31=makeQuery(id+"F2.opExtrude","SWEPT_EDGE",EDGE,{"disambiguationData":[OSD([sQuery(id+"F0.wireOp",EDGE,"E2"),sQuery(id+"F0.wireOp",EDGE,"E12.5.1"),sQuery(id+"F0.wireOp",EDGE,"E12.5.2")])]});
            var Q32;
            Q32=makeQuery(id+"F2.opExtrude","SWEPT_EDGE",EDGE,{"disambiguationData":[OSD([sQuery(id+"F0.wireOp",EDGE,"E2"),sQuery(id+"F0.wireOp",EDGE,"E12.4.1"),sQuery(id+"F0.wireOp",EDGE,"E12.4.2")])]});
            var Q33;
            Q33=makeQuery(id+"F2.opExtrude","SWEPT_EDGE",EDGE,{"disambiguationData":[OSD([sQuery(id+"F0.wireOp",EDGE,"E2"),sQuery(id+"F0.wireOp",EDGE,"E12.3.1"),sQuery(id+"F0.wireOp",EDGE,"E12.3.2")])]});
            fillet(context, id + "F3", {"entities" : qUnion([Q0, Q1, Q2, Q3, Q4, Q5, Q6, Q7, Q8, Q9, Q10, Q11, Q12, Q13, Q14, Q15, Q16, Q17, Q18, Q19, Q20, Q21, Q22, Q23, Q24, Q25, Q26, Q27, Q28, Q29, Q30, Q31, Q32, Q33]), "radius" : 5.08 * mm, "tangentPropagation" : true, "allowEdgeOverflow" : false});
        }
        {
            var Q0;
            Q0=makeQuery(id+"F2.opExtrude","SWEPT_EDGE",EDGE,{"disambiguationData":[OSD([sQuery(id+"F0.wireOp",EDGE,"E4"),sQuery(id+"F0.wireOp",EDGE,"E8")])]});
            var Q1;
            Q1=makeQuery(id+"F2.opExtrude","SWEPT_EDGE",EDGE,{"disambiguationData":[OSD([sQuery(id+"F0.wireOp",EDGE,"E5"),sQuery(id+"F0.wireOp",EDGE,"E9")])]});
            var Q2;
            Q2=makeQuery(id+"F2.opExtrude","SWEPT_EDGE",EDGE,{"disambiguationData":[OSD([sQuery(id+"F0.wireOp",EDGE,"E12.1.0"),sQuery(id+"F0.wireOp",EDGE,"E12.1.1")])]});
            var Q3;
            Q3=makeQuery(id+"F2.opExtrude","SWEPT_EDGE",EDGE,{"disambiguationData":[OSD([sQuery(id+"F0.wireOp",EDGE,"E12.1.2"),sQuery(id+"F0.wireOp",EDGE,"E12.1.3")])]});
            var Q4;
            Q4=makeQuery(id+"F2.opExtrude","SWEPT_EDGE",EDGE,{"disambiguationData":[OSD([sQuery(id+"F0.wireOp",EDGE,"E12.13.2"),sQuery(id+"F0.wireOp",EDGE,"E12.13.3")])]});
            var Q5;
            Q5=makeQuery(id+"F2.opExtrude","SWEPT_EDGE",EDGE,{"disambiguationData":[OSD([sQuery(id+"F0.wireOp",EDGE,"E12.13.0"),sQuery(id+"F0.wireOp",EDGE,"E12.13.1")])]});
            var Q6;
            Q6=makeQuery(id+"F2.opExtrude","SWEPT_EDGE",EDGE,{"disambiguationData":[OSD([sQuery(id+"F0.wireOp",EDGE,"E12.2.0"),sQuery(id+"F0.wireOp",EDGE,"E12.2.1")])]});
            var Q7;
            Q7=makeQuery(id+"F2.opExtrude","SWEPT_EDGE",EDGE,{"disambiguationData":[OSD([sQuery(id+"F0.wireOp",EDGE,"E12.2.2"),sQuery(id+"F0.wireOp",EDGE,"E12.2.3")])]});
            var Q8;
            Q8=makeQuery(id+"F2.opExtrude","SWEPT_EDGE",EDGE,{"disambiguationData":[OSD([sQuery(id+"F0.wireOp",EDGE,"E12.3.0"),sQuery(id+"F0.wireOp",EDGE,"E12.3.1")])]});
            var Q9;
            Q9=makeQuery(id+"F2.opExtrude","SWEPT_EDGE",EDGE,{"disambiguationData":[OSD([sQuery(id+"F0.wireOp",EDGE,"E12.3.2"),sQuery(id+"F0.wireOp",EDGE,"E12.3.3")])]});
            var Q10;
            Q10=makeQuery(id+"F2.opExtrude","SWEPT_EDGE",EDGE,{"disambiguationData":[OSD([sQuery(id+"F0.wireOp",EDGE,"E12.4.0"),sQuery(id+"F0.wireOp",EDGE,"E12.4.1")])]});
            var Q11;
            Q11=makeQuery(id+"F2.opExtrude","SWEPT_EDGE",EDGE,{"disambiguationData":[OSD([sQuery(id+"F0.wireOp",EDGE,"E12.4.2"),sQuery(id+"F0.wireOp",EDGE,"E12.4.3")])]});
            var Q12;
            Q12=makeQuery(id+"F2.opExtrude","SWEPT_EDGE",EDGE,{"disambiguationData":[OSD([sQuery(id+"F0.wireOp",EDGE,"E12.5.0"),sQuery(id+"F0.wireOp",EDGE,"E12.5.1")])]});
            var Q13;
            Q13=makeQuery(id+"F2.opExtrude","SWEPT_EDGE",EDGE,{"disambiguationData":[OSD([sQuery(id+"F0.wireOp",EDGE,"E12.5.2"),sQuery(id+"F0.wireOp",EDGE,"E12.5.3")])]});
            var Q14;
            Q14=makeQuery(id+"F2.opExtrude","SWEPT_EDGE",EDGE,{"disambiguationData":[OSD([sQuery(id+"F0.wireOp",EDGE,"E12.6.0"),sQuery(id+"F0.wireOp",EDGE,"E12.6.1")])]});
            var Q15;
            Q15=makeQuery(id+"F2.opExtrude","SWEPT_EDGE",EDGE,{"disambiguationData":[OSD([sQuery(id+"F0.wireOp",EDGE,"E12.6.2"),sQuery(id+"F0.wireOp",EDGE,"E12.6.3")])]});
            var Q16;
            Q16=makeQuery(id+"F2.opExtrude","SWEPT_EDGE",EDGE,{"disambiguationData":[OSD([sQuery(id+"F0.wireOp",EDGE,"E12.7.0"),sQuery(id+"F0.wireOp",EDGE,"E12.7.1")])]});
            var Q17;
            Q17=makeQuery(id+"F2.opExtrude","SWEPT_EDGE",EDGE,{"disambiguationData":[OSD([sQuery(id+"F0.wireOp",EDGE,"E12.7.2"),sQuery(id+"F0.wireOp",EDGE,"E12.7.3")])]});
            var Q18;
            Q18=makeQuery(id+"F2.opExtrude","SWEPT_EDGE",EDGE,{"disambiguationData":[OSD([sQuery(id+"F0.wireOp",EDGE,"E12.8.0"),sQuery(id+"F0.wireOp",EDGE,"E12.8.1")])]});
            var Q19;
            Q19=makeQuery(id+"F2.opExtrude","SWEPT_EDGE",EDGE,{"disambiguationData":[OSD([sQuery(id+"F0.wireOp",EDGE,"E12.8.2"),sQuery(id+"F0.wireOp",EDGE,"E12.8.3")])]});
            var Q20;
            Q20=makeQuery(id+"F2.opExtrude","SWEPT_EDGE",EDGE,{"disambiguationData":[OSD([sQuery(id+"F0.wireOp",EDGE,"E12.9.0"),sQuery(id+"F0.wireOp",EDGE,"E12.9.1")])]});
            var Q21;
            Q21=makeQuery(id+"F2.opExtrude","SWEPT_EDGE",EDGE,{"disambiguationData":[OSD([sQuery(id+"F0.wireOp",EDGE,"E12.10.0"),sQuery(id+"F0.wireOp",EDGE,"E12.10.1")])]});
            var Q22;
            Q22=makeQuery(id+"F2.opExtrude","SWEPT_EDGE",EDGE,{"disambiguationData":[OSD([sQuery(id+"F0.wireOp",EDGE,"E12.9.2"),sQuery(id+"F0.wireOp",EDGE,"E12.9.3")])]});
            var Q23;
            Q23=makeQuery(id+"F2.opExtrude","SWEPT_EDGE",EDGE,{"disambiguationData":[OSD([sQuery(id+"F0.wireOp",EDGE,"E12.10.2"),sQuery(id+"F0.wireOp",EDGE,"E12.10.3")])]});
            var Q24;
            Q24=makeQuery(id+"F2.opExtrude","SWEPT_EDGE",EDGE,{"disambiguationData":[OSD([sQuery(id+"F0.wireOp",EDGE,"E12.11.0"),sQuery(id+"F0.wireOp",EDGE,"E12.11.1")])]});
            var Q25;
            Q25=makeQuery(id+"F2.opExtrude","SWEPT_EDGE",EDGE,{"disambiguationData":[OSD([sQuery(id+"F0.wireOp",EDGE,"E12.11.2"),sQuery(id+"F0.wireOp",EDGE,"E12.11.3")])]});
            var Q26;
            Q26=makeQuery(id+"F2.opExtrude","SWEPT_EDGE",EDGE,{"disambiguationData":[OSD([sQuery(id+"F0.wireOp",EDGE,"E12.12.0"),sQuery(id+"F0.wireOp",EDGE,"E12.12.1")])]});
            var Q27;
            Q27=makeQuery(id+"F2.opExtrude","SWEPT_EDGE",EDGE,{"disambiguationData":[OSD([sQuery(id+"F0.wireOp",EDGE,"E12.12.2"),sQuery(id+"F0.wireOp",EDGE,"E12.12.3")])]});
            fillet(context, id + "F4", {"entities" : qUnion([Q0, Q1, Q2, Q3, Q4, Q5, Q6, Q7, Q8, Q9, Q10, Q11, Q12, Q13, Q14, Q15, Q16, Q17, Q18, Q19, Q20, Q21, Q22, Q23, Q24, Q25, Q26, Q27]), "radius" : 1.02 * mm, "tangentPropagation" : true, "allowEdgeOverflow" : false});
        }
        {
            var Q0;
            Q0=makeQuery(id+"F1.opExtrude","SWEPT_EDGE",EDGE,{"disambiguationData":[OSD([sQuery(id+"F0.wireOp",EDGE,"E6"),sQuery(id+"F0.wireOp",EDGE,"E11")])]});
            var Q1;
            Q1=makeQuery(id+"F1.opExtrude","SWEPT_EDGE",EDGE,{"disambiguationData":[OSD([sQuery(id+"F0.wireOp",EDGE,"E7"),sQuery(id+"F0.wireOp",EDGE,"E10")])]});
            var Q2;
            Q2=makeQuery(id+"F1.opExtrude","SWEPT_EDGE",EDGE,{"disambiguationData":[OSD([sQuery(id+"F0.wireOp",EDGE,"E13.19.2"),sQuery(id+"F0.wireOp",EDGE,"E13.19.3")])]});
            var Q3;
            Q3=makeQuery(id+"F1.opExtrude","SWEPT_EDGE",EDGE,{"disambiguationData":[OSD([sQuery(id+"F0.wireOp",EDGE,"E13.1.0"),sQuery(id+"F0.wireOp",EDGE,"E13.1.1")])]});
            var Q4;
            Q4=makeQuery(id+"F1.opExtrude","SWEPT_EDGE",EDGE,{"disambiguationData":[OSD([sQuery(id+"F0.wireOp",EDGE,"E13.1.2"),sQuery(id+"F0.wireOp",EDGE,"E13.1.3")])]});
            var Q5;
            Q5=makeQuery(id+"F1.opExtrude","SWEPT_EDGE",EDGE,{"disambiguationData":[OSD([sQuery(id+"F0.wireOp",EDGE,"E13.19.0"),sQuery(id+"F0.wireOp",EDGE,"E13.19.1")])]});
            var Q6;
            Q6=makeQuery(id+"F1.opExtrude","SWEPT_EDGE",EDGE,{"disambiguationData":[OSD([sQuery(id+"F0.wireOp",EDGE,"E13.2.0"),sQuery(id+"F0.wireOp",EDGE,"E13.2.1")])]});
            var Q7;
            Q7=makeQuery(id+"F1.opExtrude","SWEPT_EDGE",EDGE,{"disambiguationData":[OSD([sQuery(id+"F0.wireOp",EDGE,"E13.2.2"),sQuery(id+"F0.wireOp",EDGE,"E13.2.3")])]});
            var Q8;
            Q8=makeQuery(id+"F1.opExtrude","SWEPT_EDGE",EDGE,{"disambiguationData":[OSD([sQuery(id+"F0.wireOp",EDGE,"E13.3.0"),sQuery(id+"F0.wireOp",EDGE,"E13.3.1")])]});
            var Q9;
            Q9=makeQuery(id+"F1.opExtrude","SWEPT_EDGE",EDGE,{"disambiguationData":[OSD([sQuery(id+"F0.wireOp",EDGE,"E13.3.2"),sQuery(id+"F0.wireOp",EDGE,"E13.3.3")])]});
            var Q10;
            Q10=makeQuery(id+"F1.opExtrude","SWEPT_EDGE",EDGE,{"disambiguationData":[OSD([sQuery(id+"F0.wireOp",EDGE,"E13.4.0"),sQuery(id+"F0.wireOp",EDGE,"E13.4.1")])]});
            var Q11;
            Q11=makeQuery(id+"F1.opExtrude","SWEPT_EDGE",EDGE,{"disambiguationData":[OSD([sQuery(id+"F0.wireOp",EDGE,"E13.4.2"),sQuery(id+"F0.wireOp",EDGE,"E13.4.3")])]});
            var Q12;
            Q12=makeQuery(id+"F1.opExtrude","SWEPT_EDGE",EDGE,{"disambiguationData":[OSD([sQuery(id+"F0.wireOp",EDGE,"E13.5.0"),sQuery(id+"F0.wireOp",EDGE,"E13.5.1")])]});
            var Q13;
            Q13=makeQuery(id+"F1.opExtrude","SWEPT_EDGE",EDGE,{"disambiguationData":[OSD([sQuery(id+"F0.wireOp",EDGE,"E13.5.2"),sQuery(id+"F0.wireOp",EDGE,"E13.5.3")])]});
            var Q14;
            Q14=makeQuery(id+"F1.opExtrude","SWEPT_EDGE",EDGE,{"disambiguationData":[OSD([sQuery(id+"F0.wireOp",EDGE,"E13.6.0"),sQuery(id+"F0.wireOp",EDGE,"E13.6.1")])]});
            var Q15;
            Q15=makeQuery(id+"F1.opExtrude","SWEPT_EDGE",EDGE,{"disambiguationData":[OSD([sQuery(id+"F0.wireOp",EDGE,"E13.6.2"),sQuery(id+"F0.wireOp",EDGE,"E13.6.3")])]});
            var Q16;
            Q16=makeQuery(id+"F1.opExtrude","SWEPT_EDGE",EDGE,{"disambiguationData":[OSD([sQuery(id+"F0.wireOp",EDGE,"E13.7.0"),sQuery(id+"F0.wireOp",EDGE,"E13.7.1")])]});
            var Q17;
            Q17=makeQuery(id+"F1.opExtrude","SWEPT_EDGE",EDGE,{"disambiguationData":[OSD([sQuery(id+"F0.wireOp",EDGE,"E13.7.2"),sQuery(id+"F0.wireOp",EDGE,"E13.7.3")])]});
            var Q18;
            Q18=makeQuery(id+"F1.opExtrude","SWEPT_EDGE",EDGE,{"disambiguationData":[OSD([sQuery(id+"F0.wireOp",EDGE,"E13.8.0"),sQuery(id+"F0.wireOp",EDGE,"E13.8.1")])]});
            var Q19;
            Q19=makeQuery(id+"F1.opExtrude","SWEPT_EDGE",EDGE,{"disambiguationData":[OSD([sQuery(id+"F0.wireOp",EDGE,"E13.8.2"),sQuery(id+"F0.wireOp",EDGE,"E13.8.3")])]});
            var Q20;
            Q20=makeQuery(id+"F1.opExtrude","SWEPT_EDGE",EDGE,{"disambiguationData":[OSD([sQuery(id+"F0.wireOp",EDGE,"E13.9.0"),sQuery(id+"F0.wireOp",EDGE,"E13.9.1")])]});
            var Q21;
            Q21=makeQuery(id+"F1.opExtrude","SWEPT_EDGE",EDGE,{"disambiguationData":[OSD([sQuery(id+"F0.wireOp",EDGE,"E13.9.2"),sQuery(id+"F0.wireOp",EDGE,"E13.9.3")])]});
            var Q22;
            Q22=makeQuery(id+"F1.opExtrude","SWEPT_EDGE",EDGE,{"disambiguationData":[OSD([sQuery(id+"F0.wireOp",EDGE,"E13.10.0"),sQuery(id+"F0.wireOp",EDGE,"E13.10.1")])]});
            var Q23;
            Q23=makeQuery(id+"F1.opExtrude","SWEPT_EDGE",EDGE,{"disambiguationData":[OSD([sQuery(id+"F0.wireOp",EDGE,"E13.10.2"),sQuery(id+"F0.wireOp",EDGE,"E13.10.3")])]});
            var Q24;
            Q24=makeQuery(id+"F1.opExtrude","SWEPT_EDGE",EDGE,{"disambiguationData":[OSD([sQuery(id+"F0.wireOp",EDGE,"E13.11.0"),sQuery(id+"F0.wireOp",EDGE,"E13.11.1")])]});
            var Q25;
            Q25=makeQuery(id+"F1.opExtrude","SWEPT_EDGE",EDGE,{"disambiguationData":[OSD([sQuery(id+"F0.wireOp",EDGE,"E13.11.2"),sQuery(id+"F0.wireOp",EDGE,"E13.11.3")])]});
            var Q26;
            Q26=makeQuery(id+"F1.opExtrude","SWEPT_EDGE",EDGE,{"disambiguationData":[OSD([sQuery(id+"F0.wireOp",EDGE,"E13.12.0"),sQuery(id+"F0.wireOp",EDGE,"E13.12.1")])]});
            var Q27;
            Q27=makeQuery(id+"F1.opExtrude","SWEPT_EDGE",EDGE,{"disambiguationData":[OSD([sQuery(id+"F0.wireOp",EDGE,"E13.12.2"),sQuery(id+"F0.wireOp",EDGE,"E13.12.3")])]});
            var Q28;
            Q28=makeQuery(id+"F1.opExtrude","SWEPT_EDGE",EDGE,{"disambiguationData":[OSD([sQuery(id+"F0.wireOp",EDGE,"E13.13.0"),sQuery(id+"F0.wireOp",EDGE,"E13.13.1")])]});
            var Q29;
            Q29=makeQuery(id+"F1.opExtrude","SWEPT_EDGE",EDGE,{"disambiguationData":[OSD([sQuery(id+"F0.wireOp",EDGE,"E13.13.2"),sQuery(id+"F0.wireOp",EDGE,"E13.13.3")])]});
            var Q30;
            Q30=makeQuery(id+"F1.opExtrude","SWEPT_EDGE",EDGE,{"disambiguationData":[OSD([sQuery(id+"F0.wireOp",EDGE,"E13.14.0"),sQuery(id+"F0.wireOp",EDGE,"E13.14.1")])]});
            var Q31;
            Q31=makeQuery(id+"F1.opExtrude","SWEPT_EDGE",EDGE,{"disambiguationData":[OSD([sQuery(id+"F0.wireOp",EDGE,"E13.14.2"),sQuery(id+"F0.wireOp",EDGE,"E13.14.3")])]});
            var Q32;
            Q32=makeQuery(id+"F1.opExtrude","SWEPT_EDGE",EDGE,{"disambiguationData":[OSD([sQuery(id+"F0.wireOp",EDGE,"E13.15.0"),sQuery(id+"F0.wireOp",EDGE,"E13.15.1")])]});
            var Q33;
            Q33=makeQuery(id+"F1.opExtrude","SWEPT_EDGE",EDGE,{"disambiguationData":[OSD([sQuery(id+"F0.wireOp",EDGE,"E13.15.2"),sQuery(id+"F0.wireOp",EDGE,"E13.15.3")])]});
            var Q34;
            Q34=makeQuery(id+"F1.opExtrude","SWEPT_EDGE",EDGE,{"disambiguationData":[OSD([sQuery(id+"F0.wireOp",EDGE,"E13.16.2"),sQuery(id+"F0.wireOp",EDGE,"E13.16.3")])]});
            var Q35;
            Q35=makeQuery(id+"F1.opExtrude","SWEPT_EDGE",EDGE,{"disambiguationData":[OSD([sQuery(id+"F0.wireOp",EDGE,"E13.17.0"),sQuery(id+"F0.wireOp",EDGE,"E13.17.1")])]});
            var Q36;
            Q36=makeQuery(id+"F1.opExtrude","SWEPT_EDGE",EDGE,{"disambiguationData":[OSD([sQuery(id+"F0.wireOp",EDGE,"E13.17.2"),sQuery(id+"F0.wireOp",EDGE,"E13.17.3")])]});
            var Q37;
            Q37=makeQuery(id+"F1.opExtrude","SWEPT_EDGE",EDGE,{"disambiguationData":[OSD([sQuery(id+"F0.wireOp",EDGE,"E13.18.0"),sQuery(id+"F0.wireOp",EDGE,"E13.18.1")])]});
            var Q38;
            Q38=makeQuery(id+"F1.opExtrude","SWEPT_EDGE",EDGE,{"disambiguationData":[OSD([sQuery(id+"F0.wireOp",EDGE,"E13.18.2"),sQuery(id+"F0.wireOp",EDGE,"E13.18.3")])]});
            var Q39;
            Q39=makeQuery(id+"F1.opExtrude","SWEPT_EDGE",EDGE,{"disambiguationData":[OSD([sQuery(id+"F0.wireOp",EDGE,"E13.16.0"),sQuery(id+"F0.wireOp",EDGE,"E13.16.1")])]});
            fillet(context, id + "F5", {"entities" : qUnion([Q0, Q1, Q2, Q3, Q4, Q5, Q6, Q7, Q8, Q9, Q10, Q11, Q12, Q13, Q14, Q15, Q16, Q17, Q18, Q19, Q20, Q21, Q22, Q23, Q24, Q25, Q26, Q27, Q28, Q29, Q30, Q31, Q32, Q33, Q34, Q35, Q36, Q37, Q38, Q39]), "radius" : 1.02 * mm, "tangentPropagation" : true, "allowEdgeOverflow" : false});
        }
        {
            var Q0;
            Q0=makeQuery(id+"F2.opExtrude","SWEPT_EDGE",EDGE,{"disambiguationData":[OSD([sQuery(id+"F0.wireOp",EDGE,"E2"),sQuery(id+"F0.wireOp",EDGE,"E4")])]});
            var Q1;
            Q1=makeQuery(id+"F2.opExtrude","SWEPT_EDGE",EDGE,{"disambiguationData":[OSD([sQuery(id+"F0.wireOp",EDGE,"E2"),sQuery(id+"F0.wireOp",EDGE,"E12.1.0")])]});
            var Q2;
            Q2=makeQuery(id+"F2.opExtrude","SWEPT_EDGE",EDGE,{"disambiguationData":[OSD([sQuery(id+"F0.wireOp",EDGE,"E2"),sQuery(id+"F0.wireOp",EDGE,"E12.1.3")])]});
            var Q3;
            Q3=makeQuery(id+"F2.opExtrude","SWEPT_EDGE",EDGE,{"disambiguationData":[OSD([sQuery(id+"F0.wireOp",EDGE,"E2"),sQuery(id+"F0.wireOp",EDGE,"E5")])]});
            var Q4;
            Q4=makeQuery(id+"F2.opExtrude","SWEPT_EDGE",EDGE,{"disambiguationData":[OSD([sQuery(id+"F0.wireOp",EDGE,"E2"),sQuery(id+"F0.wireOp",EDGE,"E12.13.3")])]});
            var Q5;
            Q5=makeQuery(id+"F2.opExtrude","SWEPT_EDGE",EDGE,{"disambiguationData":[OSD([sQuery(id+"F0.wireOp",EDGE,"E2"),sQuery(id+"F0.wireOp",EDGE,"E12.13.0")])]});
            var Q6;
            Q6=makeQuery(id+"F2.opExtrude","SWEPT_EDGE",EDGE,{"disambiguationData":[OSD([sQuery(id+"F0.wireOp",EDGE,"E2"),sQuery(id+"F0.wireOp",EDGE,"E12.2.0")])]});
            var Q7;
            Q7=makeQuery(id+"F2.opExtrude","SWEPT_EDGE",EDGE,{"disambiguationData":[OSD([sQuery(id+"F0.wireOp",EDGE,"E2"),sQuery(id+"F0.wireOp",EDGE,"E12.2.3")])]});
            var Q8;
            Q8=makeQuery(id+"F2.opExtrude","SWEPT_EDGE",EDGE,{"disambiguationData":[OSD([sQuery(id+"F0.wireOp",EDGE,"E2"),sQuery(id+"F0.wireOp",EDGE,"E12.3.0")])]});
            var Q9;
            Q9=makeQuery(id+"F2.opExtrude","SWEPT_EDGE",EDGE,{"disambiguationData":[OSD([sQuery(id+"F0.wireOp",EDGE,"E2"),sQuery(id+"F0.wireOp",EDGE,"E12.12.3")])]});
            var Q10;
            Q10=makeQuery(id+"F2.opExtrude","SWEPT_EDGE",EDGE,{"disambiguationData":[OSD([sQuery(id+"F0.wireOp",EDGE,"E2"),sQuery(id+"F0.wireOp",EDGE,"E12.12.0")])]});
            var Q11;
            Q11=makeQuery(id+"F2.opExtrude","SWEPT_EDGE",EDGE,{"disambiguationData":[OSD([sQuery(id+"F0.wireOp",EDGE,"E2"),sQuery(id+"F0.wireOp",EDGE,"E12.11.3")])]});
            var Q12;
            Q12=makeQuery(id+"F2.opExtrude","SWEPT_EDGE",EDGE,{"disambiguationData":[OSD([sQuery(id+"F0.wireOp",EDGE,"E2"),sQuery(id+"F0.wireOp",EDGE,"E12.3.3")])]});
            var Q13;
            Q13=makeQuery(id+"F2.opExtrude","SWEPT_EDGE",EDGE,{"disambiguationData":[OSD([sQuery(id+"F0.wireOp",EDGE,"E2"),sQuery(id+"F0.wireOp",EDGE,"E12.4.0")])]});
            var Q14;
            Q14=makeQuery(id+"F2.opExtrude","SWEPT_EDGE",EDGE,{"disambiguationData":[OSD([sQuery(id+"F0.wireOp",EDGE,"E2"),sQuery(id+"F0.wireOp",EDGE,"E12.4.3")])]});
            var Q15;
            Q15=makeQuery(id+"F2.opExtrude","SWEPT_EDGE",EDGE,{"disambiguationData":[OSD([sQuery(id+"F0.wireOp",EDGE,"E2"),sQuery(id+"F0.wireOp",EDGE,"E12.5.0")])]});
            var Q16;
            Q16=makeQuery(id+"F2.opExtrude","SWEPT_EDGE",EDGE,{"disambiguationData":[OSD([sQuery(id+"F0.wireOp",EDGE,"E2"),sQuery(id+"F0.wireOp",EDGE,"E12.5.3")])]});
            var Q17;
            Q17=makeQuery(id+"F2.opExtrude","SWEPT_EDGE",EDGE,{"disambiguationData":[OSD([sQuery(id+"F0.wireOp",EDGE,"E2"),sQuery(id+"F0.wireOp",EDGE,"E12.6.0")])]});
            var Q18;
            Q18=makeQuery(id+"F2.opExtrude","SWEPT_EDGE",EDGE,{"disambiguationData":[OSD([sQuery(id+"F0.wireOp",EDGE,"E2"),sQuery(id+"F0.wireOp",EDGE,"E12.6.3")])]});
            var Q19;
            Q19=makeQuery(id+"F2.opExtrude","SWEPT_EDGE",EDGE,{"disambiguationData":[OSD([sQuery(id+"F0.wireOp",EDGE,"E2"),sQuery(id+"F0.wireOp",EDGE,"E12.7.0")])]});
            var Q20;
            Q20=makeQuery(id+"F2.opExtrude","SWEPT_EDGE",EDGE,{"disambiguationData":[OSD([sQuery(id+"F0.wireOp",EDGE,"E2"),sQuery(id+"F0.wireOp",EDGE,"E12.7.3")])]});
            var Q21;
            Q21=makeQuery(id+"F2.opExtrude","SWEPT_EDGE",EDGE,{"disambiguationData":[OSD([sQuery(id+"F0.wireOp",EDGE,"E2"),sQuery(id+"F0.wireOp",EDGE,"E12.8.0")])]});
            var Q22;
            Q22=makeQuery(id+"F2.opExtrude","SWEPT_EDGE",EDGE,{"disambiguationData":[OSD([sQuery(id+"F0.wireOp",EDGE,"E2"),sQuery(id+"F0.wireOp",EDGE,"E12.8.3")])]});
            var Q23;
            Q23=makeQuery(id+"F2.opExtrude","SWEPT_EDGE",EDGE,{"disambiguationData":[OSD([sQuery(id+"F0.wireOp",EDGE,"E2"),sQuery(id+"F0.wireOp",EDGE,"E12.9.0")])]});
            var Q24;
            Q24=makeQuery(id+"F2.opExtrude","SWEPT_EDGE",EDGE,{"disambiguationData":[OSD([sQuery(id+"F0.wireOp",EDGE,"E2"),sQuery(id+"F0.wireOp",EDGE,"E12.9.3")])]});
            var Q25;
            Q25=makeQuery(id+"F2.opExtrude","SWEPT_EDGE",EDGE,{"disambiguationData":[OSD([sQuery(id+"F0.wireOp",EDGE,"E2"),sQuery(id+"F0.wireOp",EDGE,"E12.10.0")])]});
            var Q26;
            Q26=makeQuery(id+"F2.opExtrude","SWEPT_EDGE",EDGE,{"disambiguationData":[OSD([sQuery(id+"F0.wireOp",EDGE,"E2"),sQuery(id+"F0.wireOp",EDGE,"E12.10.3")])]});
            var Q27;
            Q27=makeQuery(id+"F2.opExtrude","SWEPT_EDGE",EDGE,{"disambiguationData":[OSD([sQuery(id+"F0.wireOp",EDGE,"E2"),sQuery(id+"F0.wireOp",EDGE,"E12.11.0")])]});
            fillet(context, id + "F6", {"entities" : qUnion([Q0, Q1, Q2, Q3, Q4, Q5, Q6, Q7, Q8, Q9, Q10, Q11, Q12, Q13, Q14, Q15, Q16, Q17, Q18, Q19, Q20, Q21, Q22, Q23, Q24, Q25, Q26, Q27]), "radius" : 0.76 * mm, "tangentPropagation" : true, "allowEdgeOverflow" : false});
        }
        {
            var Q0;
            Q0=makeQuery(id+"F1.opExtrude","SWEPT_EDGE",EDGE,{"disambiguationData":[OSD([sQuery(id+"F0.wireOp",EDGE,"E1"),sQuery(id+"F0.wireOp",EDGE,"E13.1.3")])]});
            var Q1;
            Q1=makeQuery(id+"F1.opExtrude","SWEPT_EDGE",EDGE,{"disambiguationData":[OSD([sQuery(id+"F0.wireOp",EDGE,"E1"),sQuery(id+"F0.wireOp",EDGE,"E13.1.0")])]});
            var Q2;
            Q2=makeQuery(id+"F1.opExtrude","SWEPT_EDGE",EDGE,{"disambiguationData":[OSD([sQuery(id+"F0.wireOp",EDGE,"E1"),sQuery(id+"F0.wireOp",EDGE,"E6")])]});
            var Q3;
            Q3=makeQuery(id+"F1.opExtrude","SWEPT_EDGE",EDGE,{"disambiguationData":[OSD([sQuery(id+"F0.wireOp",EDGE,"E1"),sQuery(id+"F0.wireOp",EDGE,"E7")])]});
            var Q4;
            Q4=makeQuery(id+"F1.opExtrude","SWEPT_EDGE",EDGE,{"disambiguationData":[OSD([sQuery(id+"F0.wireOp",EDGE,"E1"),sQuery(id+"F0.wireOp",EDGE,"E13.19.3")])]});
            var Q5;
            Q5=makeQuery(id+"F1.opExtrude","SWEPT_EDGE",EDGE,{"disambiguationData":[OSD([sQuery(id+"F0.wireOp",EDGE,"E1"),sQuery(id+"F0.wireOp",EDGE,"E13.19.0")])]});
            var Q6;
            Q6=makeQuery(id+"F1.opExtrude","SWEPT_EDGE",EDGE,{"disambiguationData":[OSD([sQuery(id+"F0.wireOp",EDGE,"E1"),sQuery(id+"F0.wireOp",EDGE,"E13.2.0")])]});
            var Q7;
            Q7=makeQuery(id+"F1.opExtrude","SWEPT_EDGE",EDGE,{"disambiguationData":[OSD([sQuery(id+"F0.wireOp",EDGE,"E1"),sQuery(id+"F0.wireOp",EDGE,"E13.2.3")])]});
            var Q8;
            Q8=makeQuery(id+"F1.opExtrude","SWEPT_EDGE",EDGE,{"disambiguationData":[OSD([sQuery(id+"F0.wireOp",EDGE,"E1"),sQuery(id+"F0.wireOp",EDGE,"E13.3.0")])]});
            var Q9;
            Q9=makeQuery(id+"F1.opExtrude","SWEPT_EDGE",EDGE,{"disambiguationData":[OSD([sQuery(id+"F0.wireOp",EDGE,"E1"),sQuery(id+"F0.wireOp",EDGE,"E13.3.3")])]});
            var Q10;
            Q10=makeQuery(id+"F1.opExtrude","SWEPT_EDGE",EDGE,{"disambiguationData":[OSD([sQuery(id+"F0.wireOp",EDGE,"E1"),sQuery(id+"F0.wireOp",EDGE,"E13.4.0")])]});
            var Q11;
            Q11=makeQuery(id+"F1.opExtrude","SWEPT_EDGE",EDGE,{"disambiguationData":[OSD([sQuery(id+"F0.wireOp",EDGE,"E1"),sQuery(id+"F0.wireOp",EDGE,"E13.18.3")])]});
            var Q12;
            Q12=makeQuery(id+"F1.opExtrude","SWEPT_EDGE",EDGE,{"disambiguationData":[OSD([sQuery(id+"F0.wireOp",EDGE,"E1"),sQuery(id+"F0.wireOp",EDGE,"E13.18.0")])]});
            var Q13;
            Q13=makeQuery(id+"F1.opExtrude","SWEPT_EDGE",EDGE,{"disambiguationData":[OSD([sQuery(id+"F0.wireOp",EDGE,"E1"),sQuery(id+"F0.wireOp",EDGE,"E13.17.3")])]});
            var Q14;
            Q14=makeQuery(id+"F1.opExtrude","SWEPT_EDGE",EDGE,{"disambiguationData":[OSD([sQuery(id+"F0.wireOp",EDGE,"E1"),sQuery(id+"F0.wireOp",EDGE,"E13.17.0")])]});
            var Q15;
            Q15=makeQuery(id+"F1.opExtrude","SWEPT_EDGE",EDGE,{"disambiguationData":[OSD([sQuery(id+"F0.wireOp",EDGE,"E1"),sQuery(id+"F0.wireOp",EDGE,"E13.16.3")])]});
            var Q16;
            Q16=makeQuery(id+"F1.opExtrude","SWEPT_EDGE",EDGE,{"disambiguationData":[OSD([sQuery(id+"F0.wireOp",EDGE,"E1"),sQuery(id+"F0.wireOp",EDGE,"E13.16.0")])]});
            var Q17;
            Q17=makeQuery(id+"F1.opExtrude","SWEPT_EDGE",EDGE,{"disambiguationData":[OSD([sQuery(id+"F0.wireOp",EDGE,"E1"),sQuery(id+"F0.wireOp",EDGE,"E13.15.3")])]});
            var Q18;
            Q18=makeQuery(id+"F1.opExtrude","SWEPT_EDGE",EDGE,{"disambiguationData":[OSD([sQuery(id+"F0.wireOp",EDGE,"E1"),sQuery(id+"F0.wireOp",EDGE,"E13.15.0")])]});
            var Q19;
            Q19=makeQuery(id+"F1.opExtrude","SWEPT_EDGE",EDGE,{"disambiguationData":[OSD([sQuery(id+"F0.wireOp",EDGE,"E1"),sQuery(id+"F0.wireOp",EDGE,"E13.14.3")])]});
            var Q20;
            Q20=makeQuery(id+"F1.opExtrude","SWEPT_EDGE",EDGE,{"disambiguationData":[OSD([sQuery(id+"F0.wireOp",EDGE,"E1"),sQuery(id+"F0.wireOp",EDGE,"E13.14.0")])]});
            var Q21;
            Q21=makeQuery(id+"F1.opExtrude","SWEPT_EDGE",EDGE,{"disambiguationData":[OSD([sQuery(id+"F0.wireOp",EDGE,"E1"),sQuery(id+"F0.wireOp",EDGE,"E13.13.3")])]});
            var Q22;
            Q22=makeQuery(id+"F1.opExtrude","SWEPT_EDGE",EDGE,{"disambiguationData":[OSD([sQuery(id+"F0.wireOp",EDGE,"E1"),sQuery(id+"F0.wireOp",EDGE,"E13.13.0")])]});
            var Q23;
            Q23=makeQuery(id+"F1.opExtrude","SWEPT_EDGE",EDGE,{"disambiguationData":[OSD([sQuery(id+"F0.wireOp",EDGE,"E1"),sQuery(id+"F0.wireOp",EDGE,"E13.12.3")])]});
            var Q24;
            Q24=makeQuery(id+"F1.opExtrude","SWEPT_EDGE",EDGE,{"disambiguationData":[OSD([sQuery(id+"F0.wireOp",EDGE,"E1"),sQuery(id+"F0.wireOp",EDGE,"E13.12.0")])]});
            var Q25;
            Q25=makeQuery(id+"F1.opExtrude","SWEPT_EDGE",EDGE,{"disambiguationData":[OSD([sQuery(id+"F0.wireOp",EDGE,"E1"),sQuery(id+"F0.wireOp",EDGE,"E13.11.3")])]});
            var Q26;
            Q26=makeQuery(id+"F1.opExtrude","SWEPT_EDGE",EDGE,{"disambiguationData":[OSD([sQuery(id+"F0.wireOp",EDGE,"E1"),sQuery(id+"F0.wireOp",EDGE,"E13.11.0")])]});
            var Q27;
            Q27=makeQuery(id+"F1.opExtrude","SWEPT_EDGE",EDGE,{"disambiguationData":[OSD([sQuery(id+"F0.wireOp",EDGE,"E1"),sQuery(id+"F0.wireOp",EDGE,"E13.10.3")])]});
            var Q28;
            Q28=makeQuery(id+"F1.opExtrude","SWEPT_EDGE",EDGE,{"disambiguationData":[OSD([sQuery(id+"F0.wireOp",EDGE,"E1"),sQuery(id+"F0.wireOp",EDGE,"E13.10.0")])]});
            var Q29;
            Q29=makeQuery(id+"F1.opExtrude","SWEPT_EDGE",EDGE,{"disambiguationData":[OSD([sQuery(id+"F0.wireOp",EDGE,"E1"),sQuery(id+"F0.wireOp",EDGE,"E13.9.3")])]});
            var Q30;
            Q30=makeQuery(id+"F1.opExtrude","SWEPT_EDGE",EDGE,{"disambiguationData":[OSD([sQuery(id+"F0.wireOp",EDGE,"E1"),sQuery(id+"F0.wireOp",EDGE,"E13.9.0")])]});
            var Q31;
            Q31=makeQuery(id+"F1.opExtrude","SWEPT_EDGE",EDGE,{"disambiguationData":[OSD([sQuery(id+"F0.wireOp",EDGE,"E1"),sQuery(id+"F0.wireOp",EDGE,"E13.8.3")])]});
            var Q32;
            Q32=makeQuery(id+"F1.opExtrude","SWEPT_EDGE",EDGE,{"disambiguationData":[OSD([sQuery(id+"F0.wireOp",EDGE,"E1"),sQuery(id+"F0.wireOp",EDGE,"E13.8.0")])]});
            var Q33;
            Q33=makeQuery(id+"F1.opExtrude","SWEPT_EDGE",EDGE,{"disambiguationData":[OSD([sQuery(id+"F0.wireOp",EDGE,"E1"),sQuery(id+"F0.wireOp",EDGE,"E13.7.3")])]});
            var Q34;
            Q34=makeQuery(id+"F1.opExtrude","SWEPT_EDGE",EDGE,{"disambiguationData":[OSD([sQuery(id+"F0.wireOp",EDGE,"E1"),sQuery(id+"F0.wireOp",EDGE,"E13.7.0")])]});
            var Q35;
            Q35=makeQuery(id+"F1.opExtrude","SWEPT_EDGE",EDGE,{"disambiguationData":[OSD([sQuery(id+"F0.wireOp",EDGE,"E1"),sQuery(id+"F0.wireOp",EDGE,"E13.6.3")])]});
            var Q36;
            Q36=makeQuery(id+"F1.opExtrude","SWEPT_EDGE",EDGE,{"disambiguationData":[OSD([sQuery(id+"F0.wireOp",EDGE,"E1"),sQuery(id+"F0.wireOp",EDGE,"E13.6.0")])]});
            var Q37;
            Q37=makeQuery(id+"F1.opExtrude","SWEPT_EDGE",EDGE,{"disambiguationData":[OSD([sQuery(id+"F0.wireOp",EDGE,"E1"),sQuery(id+"F0.wireOp",EDGE,"E13.5.3")])]});
            var Q38;
            Q38=makeQuery(id+"F1.opExtrude","SWEPT_EDGE",EDGE,{"disambiguationData":[OSD([sQuery(id+"F0.wireOp",EDGE,"E1"),sQuery(id+"F0.wireOp",EDGE,"E13.5.0")])]});
            var Q39;
            Q39=makeQuery(id+"F1.opExtrude","SWEPT_EDGE",EDGE,{"disambiguationData":[OSD([sQuery(id+"F0.wireOp",EDGE,"E1"),sQuery(id+"F0.wireOp",EDGE,"E13.4.3")])]});
            fillet(context, id + "F7", {"entities" : qUnion([Q0, Q1, Q2, Q3, Q4, Q5, Q6, Q7, Q8, Q9, Q10, Q11, Q12, Q13, Q14, Q15, Q16, Q17, Q18, Q19, Q20, Q21, Q22, Q23, Q24, Q25, Q26, Q27, Q28, Q29, Q30, Q31, Q32, Q33, Q34, Q35, Q36, Q37, Q38, Q39]), "radius" : 0.76 * mm, "tangentPropagation" : true, "allowEdgeOverflow" : false});
        }
        {
            var Q0;
            Q0=makeQuery(id+"F2.opExtrude","SWEPT_BODY",BODY,{"disambiguationData":[OSD([sQuery(id+"F0.wireOp",EDGE,"E2"),sQuery(id+"F0.wireOp",EDGE,"E3"),sQuery(id+"F0.wireOp",EDGE,"E4"),sQuery(id+"F0.wireOp",EDGE,"E5"),sQuery(id+"F0.wireOp",EDGE,"E8"),sQuery(id+"F0.wireOp",EDGE,"E9"),sQuery(id+"F0.wireOp",EDGE,"E12.1.0"),sQuery(id+"F0.wireOp",EDGE,"E12.1.1"),sQuery(id+"F0.wireOp",EDGE,"E12.1.2"),sQuery(id+"F0.wireOp",EDGE,"E12.1.3"),sQuery(id+"F0.wireOp",EDGE,"E12.2.0"),sQuery(id+"F0.wireOp",EDGE,"E12.2.1"),sQuery(id+"F0.wireOp",EDGE,"E12.2.2"),sQuery(id+"F0.wireOp",EDGE,"E12.2.3"),sQuery(id+"F0.wireOp",EDGE,"E12.3.0"),sQuery(id+"F0.wireOp",EDGE,"E12.3.1"),sQuery(id+"F0.wireOp",EDGE,"E12.3.2"),sQuery(id+"F0.wireOp",EDGE,"E12.3.3"),sQuery(id+"F0.wireOp",EDGE,"E12.4.0"),sQuery(id+"F0.wireOp",EDGE,"E12.4.1"),sQuery(id+"F0.wireOp",EDGE,"E12.4.2"),sQuery(id+"F0.wireOp",EDGE,"E12.4.3"),sQuery(id+"F0.wireOp",EDGE,"E12.5.0"),sQuery(id+"F0.wireOp",EDGE,"E12.5.1"),sQuery(id+"F0.wireOp",EDGE,"E12.5.2"),sQuery(id+"F0.wireOp",EDGE,"E12.5.3"),sQuery(id+"F0.wireOp",EDGE,"E12.6.0"),sQuery(id+"F0.wireOp",EDGE,"E12.6.1"),sQuery(id+"F0.wireOp",EDGE,"E12.6.2"),sQuery(id+"F0.wireOp",EDGE,"E12.6.3"),sQuery(id+"F0.wireOp",EDGE,"E12.7.0"),sQuery(id+"F0.wireOp",EDGE,"E12.7.1"),sQuery(id+"F0.wireOp",EDGE,"E12.7.2"),sQuery(id+"F0.wireOp",EDGE,"E12.7.3"),sQuery(id+"F0.wireOp",EDGE,"E12.8.0"),sQuery(id+"F0.wireOp",EDGE,"E12.8.1"),sQuery(id+"F0.wireOp",EDGE,"E12.8.2"),sQuery(id+"F0.wireOp",EDGE,"E12.8.3"),sQuery(id+"F0.wireOp",EDGE,"E12.9.0"),sQuery(id+"F0.wireOp",EDGE,"E12.9.1"),sQuery(id+"F0.wireOp",EDGE,"E12.9.2"),sQuery(id+"F0.wireOp",EDGE,"E12.9.3"),sQuery(id+"F0.wireOp",EDGE,"E12.10.0"),sQuery(id+"F0.wireOp",EDGE,"E12.10.1"),sQuery(id+"F0.wireOp",EDGE,"E12.10.2"),sQuery(id+"F0.wireOp",EDGE,"E12.10.3"),sQuery(id+"F0.wireOp",EDGE,"E12.11.0"),sQuery(id+"F0.wireOp",EDGE,"E12.11.1"),sQuery(id+"F0.wireOp",EDGE,"E12.11.2"),sQuery(id+"F0.wireOp",EDGE,"E12.11.3"),sQuery(id+"F0.wireOp",EDGE,"E12.12.0"),sQuery(id+"F0.wireOp",EDGE,"E12.12.1"),sQuery(id+"F0.wireOp",EDGE,"E12.12.2"),sQuery(id+"F0.wireOp",EDGE,"E12.12.3"),sQuery(id+"F0.wireOp",EDGE,"E12.13.0"),sQuery(id+"F0.wireOp",EDGE,"E12.13.1"),sQuery(id+"F0.wireOp",EDGE,"E12.13.2"),sQuery(id+"F0.wireOp",EDGE,"E12.13.3")])]});
            transform(context, id + "F8", {"entities" : qUnion([Q0]), "transformType" : TransformType.TRANSLATION_3D, "dx" : 0 * mm, "dy" : 0 * mm, "dz" : -9.5 * mm, "makeCopy" : false});
        }
        {
            var Q0;
            Q0=makeQuery(id+"F1.opExtrude","SWEPT_BODY",BODY,{"disambiguationData":[OSD([sQuery(id+"F0.wireOp",EDGE,"E0"),sQuery(id+"F0.wireOp",EDGE,"E1"),sQuery(id+"F0.wireOp",EDGE,"E6"),sQuery(id+"F0.wireOp",EDGE,"E7"),sQuery(id+"F0.wireOp",EDGE,"E10"),sQuery(id+"F0.wireOp",EDGE,"E11"),sQuery(id+"F0.wireOp",EDGE,"E13.1.0"),sQuery(id+"F0.wireOp",EDGE,"E13.1.1"),sQuery(id+"F0.wireOp",EDGE,"E13.1.2"),sQuery(id+"F0.wireOp",EDGE,"E13.1.3"),sQuery(id+"F0.wireOp",EDGE,"E13.2.0"),sQuery(id+"F0.wireOp",EDGE,"E13.2.1"),sQuery(id+"F0.wireOp",EDGE,"E13.2.2"),sQuery(id+"F0.wireOp",EDGE,"E13.2.3"),sQuery(id+"F0.wireOp",EDGE,"E13.3.0"),sQuery(id+"F0.wireOp",EDGE,"E13.3.1"),sQuery(id+"F0.wireOp",EDGE,"E13.3.2"),sQuery(id+"F0.wireOp",EDGE,"E13.3.3"),sQuery(id+"F0.wireOp",EDGE,"E13.4.0"),sQuery(id+"F0.wireOp",EDGE,"E13.4.1"),sQuery(id+"F0.wireOp",EDGE,"E13.4.2"),sQuery(id+"F0.wireOp",EDGE,"E13.4.3"),sQuery(id+"F0.wireOp",EDGE,"E13.5.0"),sQuery(id+"F0.wireOp",EDGE,"E13.5.1"),sQuery(id+"F0.wireOp",EDGE,"E13.5.2"),sQuery(id+"F0.wireOp",EDGE,"E13.5.3"),sQuery(id+"F0.wireOp",EDGE,"E13.6.0"),sQuery(id+"F0.wireOp",EDGE,"E13.6.1"),sQuery(id+"F0.wireOp",EDGE,"E13.6.2"),sQuery(id+"F0.wireOp",EDGE,"E13.6.3"),sQuery(id+"F0.wireOp",EDGE,"E13.7.0"),sQuery(id+"F0.wireOp",EDGE,"E13.7.1"),sQuery(id+"F0.wireOp",EDGE,"E13.7.2"),sQuery(id+"F0.wireOp",EDGE,"E13.7.3"),sQuery(id+"F0.wireOp",EDGE,"E13.8.0"),sQuery(id+"F0.wireOp",EDGE,"E13.8.1"),sQuery(id+"F0.wireOp",EDGE,"E13.8.2"),sQuery(id+"F0.wireOp",EDGE,"E13.8.3"),sQuery(id+"F0.wireOp",EDGE,"E13.9.0"),sQuery(id+"F0.wireOp",EDGE,"E13.9.1"),sQuery(id+"F0.wireOp",EDGE,"E13.9.2"),sQuery(id+"F0.wireOp",EDGE,"E13.9.3"),sQuery(id+"F0.wireOp",EDGE,"E13.10.0"),sQuery(id+"F0.wireOp",EDGE,"E13.10.1"),sQuery(id+"F0.wireOp",EDGE,"E13.10.2"),sQuery(id+"F0.wireOp",EDGE,"E13.10.3"),sQuery(id+"F0.wireOp",EDGE,"E13.11.0"),sQuery(id+"F0.wireOp",EDGE,"E13.11.1"),sQuery(id+"F0.wireOp",EDGE,"E13.11.2"),sQuery(id+"F0.wireOp",EDGE,"E13.11.3"),sQuery(id+"F0.wireOp",EDGE,"E13.12.0"),sQuery(id+"F0.wireOp",EDGE,"E13.12.1"),sQuery(id+"F0.wireOp",EDGE,"E13.12.2"),sQuery(id+"F0.wireOp",EDGE,"E13.12.3"),sQuery(id+"F0.wireOp",EDGE,"E13.13.0"),sQuery(id+"F0.wireOp",EDGE,"E13.13.1"),sQuery(id+"F0.wireOp",EDGE,"E13.13.2"),sQuery(id+"F0.wireOp",EDGE,"E13.13.3"),sQuery(id+"F0.wireOp",EDGE,"E13.14.0"),sQuery(id+"F0.wireOp",EDGE,"E13.14.1"),sQuery(id+"F0.wireOp",EDGE,"E13.14.2"),sQuery(id+"F0.wireOp",EDGE,"E13.14.3"),sQuery(id+"F0.wireOp",EDGE,"E13.15.0"),sQuery(id+"F0.wireOp",EDGE,"E13.15.1"),sQuery(id+"F0.wireOp",EDGE,"E13.15.2"),sQuery(id+"F0.wireOp",EDGE,"E13.15.3"),sQuery(id+"F0.wireOp",EDGE,"E13.16.0"),sQuery(id+"F0.wireOp",EDGE,"E13.16.1"),sQuery(id+"F0.wireOp",EDGE,"E13.16.2"),sQuery(id+"F0.wireOp",EDGE,"E13.16.3"),sQuery(id+"F0.wireOp",EDGE,"E13.17.0"),sQuery(id+"F0.wireOp",EDGE,"E13.17.1"),sQuery(id+"F0.wireOp",EDGE,"E13.17.2"),sQuery(id+"F0.wireOp",EDGE,"E13.17.3"),sQuery(id+"F0.wireOp",EDGE,"E13.18.0"),sQuery(id+"F0.wireOp",EDGE,"E13.18.1"),sQuery(id+"F0.wireOp",EDGE,"E13.18.2"),sQuery(id+"F0.wireOp",EDGE,"E13.18.3"),sQuery(id+"F0.wireOp",EDGE,"E13.19.0"),sQuery(id+"F0.wireOp",EDGE,"E13.19.1"),sQuery(id+"F0.wireOp",EDGE,"E13.19.2"),sQuery(id+"F0.wireOp",EDGE,"E13.19.3")])]});
            var Q1;
            Q1=makeQuery(id+"F2.opExtrude","SWEPT_BODY",BODY,{"disambiguationData":[OSD([sQuery(id+"F0.wireOp",EDGE,"E2"),sQuery(id+"F0.wireOp",EDGE,"E3"),sQuery(id+"F0.wireOp",EDGE,"E4"),sQuery(id+"F0.wireOp",EDGE,"E5"),sQuery(id+"F0.wireOp",EDGE,"E8"),sQuery(id+"F0.wireOp",EDGE,"E9"),sQuery(id+"F0.wireOp",EDGE,"E12.1.0"),sQuery(id+"F0.wireOp",EDGE,"E12.1.1"),sQuery(id+"F0.wireOp",EDGE,"E12.1.2"),sQuery(id+"F0.wireOp",EDGE,"E12.1.3"),sQuery(id+"F0.wireOp",EDGE,"E12.2.0"),sQuery(id+"F0.wireOp",EDGE,"E12.2.1"),sQuery(id+"F0.wireOp",EDGE,"E12.2.2"),sQuery(id+"F0.wireOp",EDGE,"E12.2.3"),sQuery(id+"F0.wireOp",EDGE,"E12.3.0"),sQuery(id+"F0.wireOp",EDGE,"E12.3.1"),sQuery(id+"F0.wireOp",EDGE,"E12.3.2"),sQuery(id+"F0.wireOp",EDGE,"E12.3.3"),sQuery(id+"F0.wireOp",EDGE,"E12.4.0"),sQuery(id+"F0.wireOp",EDGE,"E12.4.1"),sQuery(id+"F0.wireOp",EDGE,"E12.4.2"),sQuery(id+"F0.wireOp",EDGE,"E12.4.3"),sQuery(id+"F0.wireOp",EDGE,"E12.5.0"),sQuery(id+"F0.wireOp",EDGE,"E12.5.1"),sQuery(id+"F0.wireOp",EDGE,"E12.5.2"),sQuery(id+"F0.wireOp",EDGE,"E12.5.3"),sQuery(id+"F0.wireOp",EDGE,"E12.6.0"),sQuery(id+"F0.wireOp",EDGE,"E12.6.1"),sQuery(id+"F0.wireOp",EDGE,"E12.6.2"),sQuery(id+"F0.wireOp",EDGE,"E12.6.3"),sQuery(id+"F0.wireOp",EDGE,"E12.7.0"),sQuery(id+"F0.wireOp",EDGE,"E12.7.1"),sQuery(id+"F0.wireOp",EDGE,"E12.7.2"),sQuery(id+"F0.wireOp",EDGE,"E12.7.3"),sQuery(id+"F0.wireOp",EDGE,"E12.8.0"),sQuery(id+"F0.wireOp",EDGE,"E12.8.1"),sQuery(id+"F0.wireOp",EDGE,"E12.8.2"),sQuery(id+"F0.wireOp",EDGE,"E12.8.3"),sQuery(id+"F0.wireOp",EDGE,"E12.9.0"),sQuery(id+"F0.wireOp",EDGE,"E12.9.1"),sQuery(id+"F0.wireOp",EDGE,"E12.9.2"),sQuery(id+"F0.wireOp",EDGE,"E12.9.3"),sQuery(id+"F0.wireOp",EDGE,"E12.10.0"),sQuery(id+"F0.wireOp",EDGE,"E12.10.1"),sQuery(id+"F0.wireOp",EDGE,"E12.10.2"),sQuery(id+"F0.wireOp",EDGE,"E12.10.3"),sQuery(id+"F0.wireOp",EDGE,"E12.11.0"),sQuery(id+"F0.wireOp",EDGE,"E12.11.1"),sQuery(id+"F0.wireOp",EDGE,"E12.11.2"),sQuery(id+"F0.wireOp",EDGE,"E12.11.3"),sQuery(id+"F0.wireOp",EDGE,"E12.12.0"),sQuery(id+"F0.wireOp",EDGE,"E12.12.1"),sQuery(id+"F0.wireOp",EDGE,"E12.12.2"),sQuery(id+"F0.wireOp",EDGE,"E12.12.3"),sQuery(id+"F0.wireOp",EDGE,"E12.13.0"),sQuery(id+"F0.wireOp",EDGE,"E12.13.1"),sQuery(id+"F0.wireOp",EDGE,"E12.13.2"),sQuery(id+"F0.wireOp",EDGE,"E12.13.3")])]});
            transform(context, id + "F9", {"entities" : qUnion([Q0, Q1]), "transformType" : TransformType.TRANSLATION_3D, "dx" : 0 * mm, "dy" : 6.35 * mm, "dz" : 0 * mm, "makeCopy" : true});
        }
        {
            var Q0;
            Q0=makeQuery(id+"F9.opPattern","COPY",BODY,{"derivedFrom":makeQuery(id+"F1.opExtrude","SWEPT_BODY",BODY,{"disambiguationData":[OSD([sQuery(id+"F0.wireOp",EDGE,"E0"),sQuery(id+"F0.wireOp",EDGE,"E1"),sQuery(id+"F0.wireOp",EDGE,"E6"),sQuery(id+"F0.wireOp",EDGE,"E7"),sQuery(id+"F0.wireOp",EDGE,"E10"),sQuery(id+"F0.wireOp",EDGE,"E11"),sQuery(id+"F0.wireOp",EDGE,"E13.1.0"),sQuery(id+"F0.wireOp",EDGE,"E13.1.1"),sQuery(id+"F0.wireOp",EDGE,"E13.1.2"),sQuery(id+"F0.wireOp",EDGE,"E13.1.3"),sQuery(id+"F0.wireOp",EDGE,"E13.2.0"),sQuery(id+"F0.wireOp",EDGE,"E13.2.1"),sQuery(id+"F0.wireOp",EDGE,"E13.2.2"),sQuery(id+"F0.wireOp",EDGE,"E13.2.3"),sQuery(id+"F0.wireOp",EDGE,"E13.3.0"),sQuery(id+"F0.wireOp",EDGE,"E13.3.1"),sQuery(id+"F0.wireOp",EDGE,"E13.3.2"),sQuery(id+"F0.wireOp",EDGE,"E13.3.3"),sQuery(id+"F0.wireOp",EDGE,"E13.4.0"),sQuery(id+"F0.wireOp",EDGE,"E13.4.1"),sQuery(id+"F0.wireOp",EDGE,"E13.4.2"),sQuery(id+"F0.wireOp",EDGE,"E13.4.3"),sQuery(id+"F0.wireOp",EDGE,"E13.5.0"),sQuery(id+"F0.wireOp",EDGE,"E13.5.1"),sQuery(id+"F0.wireOp",EDGE,"E13.5.2"),sQuery(id+"F0.wireOp",EDGE,"E13.5.3"),sQuery(id+"F0.wireOp",EDGE,"E13.6.0"),sQuery(id+"F0.wireOp",EDGE,"E13.6.1"),sQuery(id+"F0.wireOp",EDGE,"E13.6.2"),sQuery(id+"F0.wireOp",EDGE,"E13.6.3"),sQuery(id+"F0.wireOp",EDGE,"E13.7.0"),sQuery(id+"F0.wireOp",EDGE,"E13.7.1"),sQuery(id+"F0.wireOp",EDGE,"E13.7.2"),sQuery(id+"F0.wireOp",EDGE,"E13.7.3"),sQuery(id+"F0.wireOp",EDGE,"E13.8.0"),sQuery(id+"F0.wireOp",EDGE,"E13.8.1"),sQuery(id+"F0.wireOp",EDGE,"E13.8.2"),sQuery(id+"F0.wireOp",EDGE,"E13.8.3"),sQuery(id+"F0.wireOp",EDGE,"E13.9.0"),sQuery(id+"F0.wireOp",EDGE,"E13.9.1"),sQuery(id+"F0.wireOp",EDGE,"E13.9.2"),sQuery(id+"F0.wireOp",EDGE,"E13.9.3"),sQuery(id+"F0.wireOp",EDGE,"E13.10.0"),sQuery(id+"F0.wireOp",EDGE,"E13.10.1"),sQuery(id+"F0.wireOp",EDGE,"E13.10.2"),sQuery(id+"F0.wireOp",EDGE,"E13.10.3"),sQuery(id+"F0.wireOp",EDGE,"E13.11.0"),sQuery(id+"F0.wireOp",EDGE,"E13.11.1"),sQuery(id+"F0.wireOp",EDGE,"E13.11.2"),sQuery(id+"F0.wireOp",EDGE,"E13.11.3"),sQuery(id+"F0.wireOp",EDGE,"E13.12.0"),sQuery(id+"F0.wireOp",EDGE,"E13.12.1"),sQuery(id+"F0.wireOp",EDGE,"E13.12.2"),sQuery(id+"F0.wireOp",EDGE,"E13.12.3"),sQuery(id+"F0.wireOp",EDGE,"E13.13.0"),sQuery(id+"F0.wireOp",EDGE,"E13.13.1"),sQuery(id+"F0.wireOp",EDGE,"E13.13.2"),sQuery(id+"F0.wireOp",EDGE,"E13.13.3"),sQuery(id+"F0.wireOp",EDGE,"E13.14.0"),sQuery(id+"F0.wireOp",EDGE,"E13.14.1"),sQuery(id+"F0.wireOp",EDGE,"E13.14.2"),sQuery(id+"F0.wireOp",EDGE,"E13.14.3"),sQuery(id+"F0.wireOp",EDGE,"E13.15.0"),sQuery(id+"F0.wireOp",EDGE,"E13.15.1"),sQuery(id+"F0.wireOp",EDGE,"E13.15.2"),sQuery(id+"F0.wireOp",EDGE,"E13.15.3"),sQuery(id+"F0.wireOp",EDGE,"E13.16.0"),sQuery(id+"F0.wireOp",EDGE,"E13.16.1"),sQuery(id+"F0.wireOp",EDGE,"E13.16.2"),sQuery(id+"F0.wireOp",EDGE,"E13.16.3"),sQuery(id+"F0.wireOp",EDGE,"E13.17.0"),sQuery(id+"F0.wireOp",EDGE,"E13.17.1"),sQuery(id+"F0.wireOp",EDGE,"E13.17.2"),sQuery(id+"F0.wireOp",EDGE,"E13.17.3"),sQuery(id+"F0.wireOp",EDGE,"E13.18.0"),sQuery(id+"F0.wireOp",EDGE,"E13.18.1"),sQuery(id+"F0.wireOp",EDGE,"E13.18.2"),sQuery(id+"F0.wireOp",EDGE,"E13.18.3"),sQuery(id+"F0.wireOp",EDGE,"E13.19.0"),sQuery(id+"F0.wireOp",EDGE,"E13.19.1"),sQuery(id+"F0.wireOp",EDGE,"E13.19.2"),sQuery(id+"F0.wireOp",EDGE,"E13.19.3")])]}),"instanceName":"1"});
            var Q1;
            Q1=makeQuery(id+"F9.opPattern","COPY",EDGE,{"derivedFrom":makeQuery(id+"F1.opExtrude","CAP_EDGE",EDGE,{"disambiguationData":[OSD([sQuery(id+"F0.wireOp",EDGE,"E0")])],"isStart":false}),"instanceName":"1"});
            transform(context, id + "F10", {"entities" : qUnion([Q0]), "transformType" : TransformType.ROTATION, "transformAxis" : qUnion([Q1]), "angle" : 9 * degree, "makeCopy" : false});
        }
        {
            var Q0;
            Q0=makeQuery(id+"F9.opPattern","COPY",BODY,{"derivedFrom":makeQuery(id+"F2.opExtrude","SWEPT_BODY",BODY,{"disambiguationData":[OSD([sQuery(id+"F0.wireOp",EDGE,"E2"),sQuery(id+"F0.wireOp",EDGE,"E3"),sQuery(id+"F0.wireOp",EDGE,"E4"),sQuery(id+"F0.wireOp",EDGE,"E5"),sQuery(id+"F0.wireOp",EDGE,"E8"),sQuery(id+"F0.wireOp",EDGE,"E9"),sQuery(id+"F0.wireOp",EDGE,"E12.1.0"),sQuery(id+"F0.wireOp",EDGE,"E12.1.1"),sQuery(id+"F0.wireOp",EDGE,"E12.1.2"),sQuery(id+"F0.wireOp",EDGE,"E12.1.3"),sQuery(id+"F0.wireOp",EDGE,"E12.2.0"),sQuery(id+"F0.wireOp",EDGE,"E12.2.1"),sQuery(id+"F0.wireOp",EDGE,"E12.2.2"),sQuery(id+"F0.wireOp",EDGE,"E12.2.3"),sQuery(id+"F0.wireOp",EDGE,"E12.3.0"),sQuery(id+"F0.wireOp",EDGE,"E12.3.1"),sQuery(id+"F0.wireOp",EDGE,"E12.3.2"),sQuery(id+"F0.wireOp",EDGE,"E12.3.3"),sQuery(id+"F0.wireOp",EDGE,"E12.4.0"),sQuery(id+"F0.wireOp",EDGE,"E12.4.1"),sQuery(id+"F0.wireOp",EDGE,"E12.4.2"),sQuery(id+"F0.wireOp",EDGE,"E12.4.3"),sQuery(id+"F0.wireOp",EDGE,"E12.5.0"),sQuery(id+"F0.wireOp",EDGE,"E12.5.1"),sQuery(id+"F0.wireOp",EDGE,"E12.5.2"),sQuery(id+"F0.wireOp",EDGE,"E12.5.3"),sQuery(id+"F0.wireOp",EDGE,"E12.6.0"),sQuery(id+"F0.wireOp",EDGE,"E12.6.1"),sQuery(id+"F0.wireOp",EDGE,"E12.6.2"),sQuery(id+"F0.wireOp",EDGE,"E12.6.3"),sQuery(id+"F0.wireOp",EDGE,"E12.7.0"),sQuery(id+"F0.wireOp",EDGE,"E12.7.1"),sQuery(id+"F0.wireOp",EDGE,"E12.7.2"),sQuery(id+"F0.wireOp",EDGE,"E12.7.3"),sQuery(id+"F0.wireOp",EDGE,"E12.8.0"),sQuery(id+"F0.wireOp",EDGE,"E12.8.1"),sQuery(id+"F0.wireOp",EDGE,"E12.8.2"),sQuery(id+"F0.wireOp",EDGE,"E12.8.3"),sQuery(id+"F0.wireOp",EDGE,"E12.9.0"),sQuery(id+"F0.wireOp",EDGE,"E12.9.1"),sQuery(id+"F0.wireOp",EDGE,"E12.9.2"),sQuery(id+"F0.wireOp",EDGE,"E12.9.3"),sQuery(id+"F0.wireOp",EDGE,"E12.10.0"),sQuery(id+"F0.wireOp",EDGE,"E12.10.1"),sQuery(id+"F0.wireOp",EDGE,"E12.10.2"),sQuery(id+"F0.wireOp",EDGE,"E12.10.3"),sQuery(id+"F0.wireOp",EDGE,"E12.11.0"),sQuery(id+"F0.wireOp",EDGE,"E12.11.1"),sQuery(id+"F0.wireOp",EDGE,"E12.11.2"),sQuery(id+"F0.wireOp",EDGE,"E12.11.3"),sQuery(id+"F0.wireOp",EDGE,"E12.12.0"),sQuery(id+"F0.wireOp",EDGE,"E12.12.1"),sQuery(id+"F0.wireOp",EDGE,"E12.12.2"),sQuery(id+"F0.wireOp",EDGE,"E12.12.3"),sQuery(id+"F0.wireOp",EDGE,"E12.13.0"),sQuery(id+"F0.wireOp",EDGE,"E12.13.1"),sQuery(id+"F0.wireOp",EDGE,"E12.13.2"),sQuery(id+"F0.wireOp",EDGE,"E12.13.3")])]}),"instanceName":"1"});
            var Q1;
            Q1=makeQuery(id+"F9.opPattern","COPY",EDGE,{"derivedFrom":makeQuery(id+"F2.opExtrude","CAP_EDGE",EDGE,{"disambiguationData":[OSD([sQuery(id+"F0.wireOp",EDGE,"E3")])],"isStart":false}),"instanceName":"1"});
            transform(context, id + "F11", {"entities" : qUnion([Q0]), "transformType" : TransformType.ROTATION, "transformAxis" : qUnion([Q1]), "angle" : 12.86 * degree, "makeCopy" : false});
        }
    });
